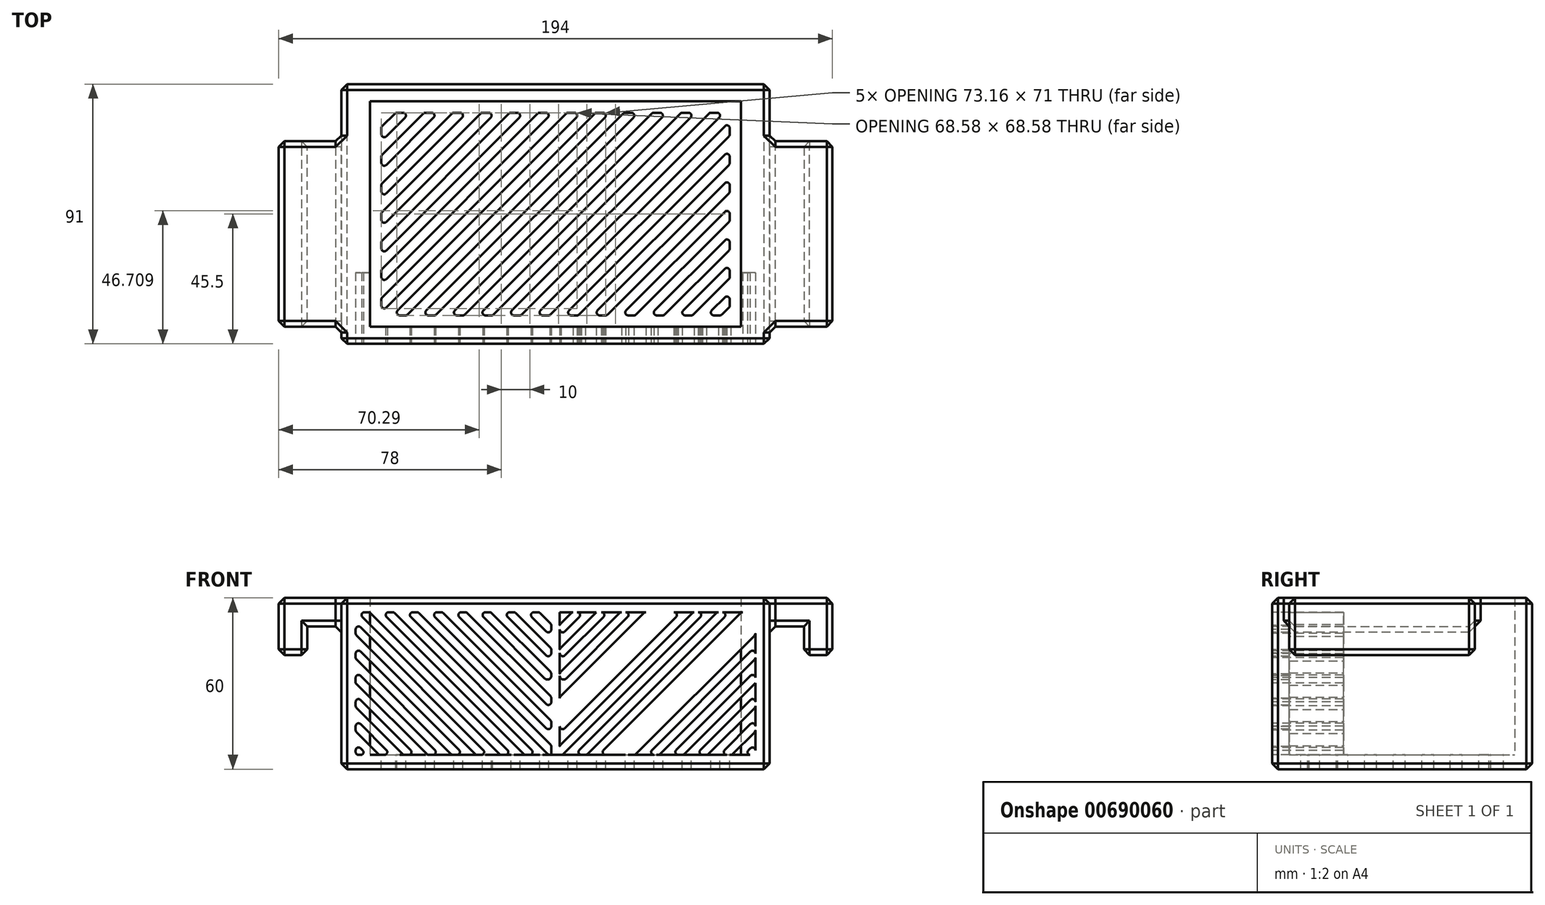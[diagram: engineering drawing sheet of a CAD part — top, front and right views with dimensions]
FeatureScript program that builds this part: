
annotation { "Feature Type Name" : "Feature", "Feature Type Description" : "" }
export const myFeature = defineFeature(function(context is Context, id is Id, definition is map)
    precondition{}
    {
        {
            var Q0;
            Q0=qCreatedBy(makeId("Top.planeOp"),FACE);
            var sketch = newSketch(context, id + "F0", { "sketchPlane" : qUnion([Q0])});
            skLineSegment(sketch, "E0", {"start": v(0, 0) * mm, "end": v(0, -65) * mm});
            skLineSegment(sketch, "E1", {"start": v(0, -65) * mm, "end": v(12, -65) * mm});
            skLineSegment(sketch, "E2", {"start": v(12, -65) * mm, "end": v(12, 0) * mm});
            skLineSegment(sketch, "E3", {"start": v(12, 0) * mm, "end": v(0, 0) * mm});
            skLineSegment(sketch, "E4", {"start": v(12, -65) * mm, "end": v(22, -65) * mm});
            skLineSegment(sketch, "E5", {"start": v(22, -65) * mm, "end": v(22, 0) * mm});
            skLineSegment(sketch, "E6", {"start": v(22, 0) * mm, "end": v(12, 0) * mm});
            skLineSegment(sketch, "E7", {"start": v(0, -65) * mm, "end": v(-10, -65) * mm});
            skLineSegment(sketch, "E8", {"start": v(-10, -65) * mm, "end": v(-10, 20) * mm});
            skLineSegment(sketch, "E9", {"start": v(-10, 20) * mm, "end": v(0, 20) * mm});
            skLineSegment(sketch, "E10", {"start": v(0, 20) * mm, "end": v(0, 0) * mm});
            skLineSegment(sketch, "E11", {"start": v(-10, 20) * mm, "end": v(-140, 20) * mm});
            skLineSegment(sketch, "E12.MirrorCS", {"start": v(-150, 0) * mm, "end": v(-150, -65) * mm});
            skLineSegment(sketch, "E13.MirrorCS", {"start": v(-150, -65) * mm, "end": v(-162, -65) * mm});
            skLineSegment(sketch, "E14.MirrorCS", {"start": v(-162, -65) * mm, "end": v(-162, 0) * mm});
            skLineSegment(sketch, "E15.MirrorCS", {"start": v(-150, 20) * mm, "end": v(-150, 0) * mm});
            skLineSegment(sketch, "E16.MirrorCS", {"start": v(-140, 20) * mm, "end": v(-150, 20) * mm});
            skLineSegment(sketch, "E17.MirrorCS", {"start": v(-140, -65) * mm, "end": v(-140, 20) * mm});
            skLineSegment(sketch, "E18.MirrorCS", {"start": v(-150, -65) * mm, "end": v(-140, -65) * mm});
            skLineSegment(sketch, "E19.MirrorCS", {"start": v(-172, 0) * mm, "end": v(-162, 0) * mm});
            skLineSegment(sketch, "E20.MirrorCS", {"start": v(-172, -65) * mm, "end": v(-172, 0) * mm});
            skLineSegment(sketch, "E21.MirrorCS", {"start": v(-162, -65) * mm, "end": v(-172, -65) * mm});
            skLineSegment(sketch, "E22.MirrorCS", {"start": v(-162, 0) * mm, "end": v(-150, 0) * mm});
            skLineSegment(sketch, "E23", {"start": v(-140, -65) * mm, "end": v(-10, -65) * mm});
            skLineSegment(sketch, "E24", {"start": v(-150, -65) * mm, "end": v(-150, -71) * mm});
            skLineSegment(sketch, "E25", {"start": v(-150, -71) * mm, "end": v(0, -71) * mm});
            skLineSegment(sketch, "E26", {"start": v(0, -71) * mm, "end": v(0, -65) * mm});
            skLineSegment(sketch, "E27", {"start": v(-140, 14) * mm, "end": v(-10, 14) * mm});
            skSolve(sketch);
        }
        {
            var Q0;
            Q0=makeQuery(id+"F0.imprint","IMPRINT",FACE,{"disambiguationData":[TD([[makeQuery(id+"F0.imprint","IMPRINT",EDGE,{"derivedFrom":sQuery(id+"F0.wireOp",EDGE,"E14.MirrorCS")}),1.0]])]});
            var Q1;
            Q1=makeQuery(id+"F0.imprint","IMPRINT",FACE,{"disambiguationData":[TD([[makeQuery(id+"F0.imprint","IMPRINT",EDGE,{"derivedFrom":sQuery(id+"F0.wireOp",EDGE,"E2")}),-1.0]])]});
            extrude(context, id + "F1", {"entities" : qUnion([Q0, Q1]), "oppositeDirection" : true, "depth" : 10 * mm, "offsetDistance" : 25 * mm, "hasSecondDirection" : true, "secondDirectionOppositeDirection" : false, "secondDirectionDepth" : 10 * mm});
        }
        {
            var Q0;
            Q0=makeQuery(id+"F0.imprint","IMPRINT",FACE,{"disambiguationData":[TD([[makeQuery(id+"F0.imprint","IMPRINT",EDGE,{"derivedFrom":sQuery(id+"F0.wireOp",EDGE,"E12.MirrorCS")}),-1.0]])]});
            var Q1;
            Q1=makeQuery(id+"F0.imprint","IMPRINT",FACE,{"disambiguationData":[TD([[makeQuery(id+"F0.imprint","IMPRINT",EDGE,{"derivedFrom":sQuery(id+"F0.wireOp",EDGE,"E0")}),1.0]])]});
            extrude(context, id + "F2", {"entities" : qUnion([Q0, Q1]), "operationType" : NewBodyOperationType.ADD, "depth" : 10 * mm, "offsetDistance" : 25 * mm});
        }
        {
            var Q0;
            Q0=makeQuery(id+"F0.imprint","IMPRINT",FACE,{"disambiguationData":[TD([[makeQuery(id+"F0.imprint","IMPRINT",EDGE,{"derivedFrom":sQuery(id+"F0.wireOp",EDGE,"E12.MirrorCS")}),1.0]])]});
            var Q1;
            Q1=makeQuery(id+"F0.imprint","IMPRINT",FACE,{"disambiguationData":[TD([[makeQuery(id+"F0.imprint","IMPRINT",EDGE,{"derivedFrom":sQuery(id+"F0.wireOp",EDGE,"E0")}),-1.0]])]});
            extrude(context, id + "F3", {"entities" : qUnion([Q0, Q1]), "operationType" : NewBodyOperationType.ADD, "depth" : 10 * mm, "offsetDistance" : 25 * mm, "hasSecondDirection" : true, "secondDirectionOppositeDirection" : true, "secondDirectionDepth" : 50 * mm});
        }
        {
            var Q0;
            Q0=makeQuery(id+"F0.imprint","IMPRINT",FACE,{"disambiguationData":[TD([[makeQuery(id+"F0.imprint","IMPRINT",EDGE,{"derivedFrom":sQuery(id+"F0.wireOp",EDGE,"E7")}),1.0]])]});
            extrude(context, id + "F4", {"entities" : qUnion([Q0]), "operationType" : NewBodyOperationType.ADD, "depth" : 10 * mm, "offsetDistance" : 25 * mm, "hasSecondDirection" : true, "secondDirectionOppositeDirection" : true, "secondDirectionDepth" : 50 * mm});
        }
        {
            var Q0;
            {var subQ0=sQuery(id+"F0.wireOp",EDGE,"E11");Q0=makeQuery(id+"F0.imprint","IMPRINT",FACE,{"disambiguationData":[TD([[makeQuery(id+"F0.imprint","IMPRINT",EDGE,{"derivedFrom":subQ0}),1.0]])]});}
            extrude(context, id + "F5", {"entities" : qUnion([Q0]), "operationType" : NewBodyOperationType.ADD, "depth" : 10 * mm, "offsetDistance" : 25 * mm, "hasSecondDirection" : true, "secondDirectionOppositeDirection" : true, "secondDirectionDepth" : 50 * mm});
        }
        {
            var Q0;
            {var subQ0=sQuery(id+"F0.wireOp",EDGE,"E23");Q0=makeQuery(id+"F0.imprint","IMPRINT",FACE,{"disambiguationData":[TD([[makeQuery(id+"F0.imprint","IMPRINT",EDGE,{"derivedFrom":subQ0}),1.0]])]});}
            extrude(context, id + "F6", {"entities" : qUnion([Q0]), "operationType" : NewBodyOperationType.ADD, "oppositeDirection" : true, "depth" : 50 * mm, "offsetDistance" : 25 * mm, "hasSecondDirection" : true, "secondDirectionOppositeDirection" : true, "secondDirectionDepth" : 45 * mm});
        }
        {
            var Q0;
            {var subQ0=sQuery(id+"F0.wireOp",EDGE,"E23");Q0=makeQuery(id+"F0.imprint","IMPRINT",FACE,{"disambiguationData":[TD([[makeQuery(id+"F0.imprint","IMPRINT",EDGE,{"derivedFrom":subQ0}),1.0]])]});}
            var sketch = newSketch(context, id + "F7", { "sketchPlane" : qUnion([Q0])});
            skLineSegment(sketch, "E28.0.0", {"start": v(-140, 14) * mm, "end": v(-140, -65) * mm});
            skLineSegment(sketch, "E28.0.1", {"start": v(-140, -65) * mm, "end": v(-10, -65) * mm});
            skLineSegment(sketch, "E28.0.2", {"start": v(-10, -65) * mm, "end": v(-10, 14) * mm});
            skLineSegment(sketch, "E28.0.3", {"start": v(-10, 14) * mm, "end": v(-140, 14) * mm});
            skLineSegment(sketch, "E29.0", {"start": v(-18.41, 10) * mm, "end": v(-20.59, 10) * mm});
            skLineSegment(sketch, "E29.1", {"start": v(-14, -58) * mm, "end": v(-14, -55.41) * mm});
            skLineSegment(sketch, "E29.2", {"start": v(-129.59, -61) * mm, "end": v(-127.41, -61) * mm});
            skLineSegment(sketch, "E29.3", {"start": v(-136, 5) * mm, "end": v(-136, 2.41) * mm});
            skLineSegment(sketch, "E30", {"start": v(-136, 5) * mm, "end": v(-131, 10) * mm});
            skLineSegment(sketch, "E31.1.0.0", {"start": v(-134.3, 1.7) * mm, "end": v(-127.7, 8.3) * mm});
            skLineSegment(sketch, "E31.2.0.0", {"start": v(-135.7, -4.7) * mm, "end": v(-121.3, 9.7) * mm});
            skLineSegment(sketch, "E31.3.0.0", {"start": v(-134.3, -8.3) * mm, "end": v(-117.7, 8.3) * mm});
            skLineSegment(sketch, "E31.4.0.0", {"start": v(-135.7, -14.7) * mm, "end": v(-111.3, 9.7) * mm});
            skLineSegment(sketch, "E31.5.0.0", {"start": v(-134.3, -18.3) * mm, "end": v(-107.7, 8.3) * mm});
            skLineSegment(sketch, "E31.6.0.0", {"start": v(-135.7, -24.7) * mm, "end": v(-101.3, 9.7) * mm});
            skLineSegment(sketch, "E31.7.0.0", {"start": v(-134.3, -28.3) * mm, "end": v(-97.7, 8.3) * mm});
            skLineSegment(sketch, "E31.8.0.0", {"start": v(-135.7, -34.7) * mm, "end": v(-91.3, 9.7) * mm});
            skLineSegment(sketch, "E31.9.0.0", {"start": v(-134.3, -38.3) * mm, "end": v(-87.7, 8.3) * mm});
            skLineSegment(sketch, "E31.10.0.0", {"start": v(-135.7, -44.7) * mm, "end": v(-81.3, 9.7) * mm});
            skLineSegment(sketch, "E31.11.0.0", {"start": v(-134.3, -48.3) * mm, "end": v(-77.7, 8.3) * mm});
            skLineSegment(sketch, "E31.12.0.0", {"start": v(-135.7, -54.7) * mm, "end": v(-71.3, 9.7) * mm});
            skLineSegment(sketch, "E31.13.0.0", {"start": v(-134.3, -58.3) * mm, "end": v(-67.7, 8.3) * mm});
            skLineSegment(sketch, "E31.14.0.0", {"start": v(-130.3, -59.3) * mm, "end": v(-61.3, 9.7) * mm});
            skLineSegment(sketch, "E31.15.0.0", {"start": v(-126.7, -60.7) * mm, "end": v(-57.7, 8.3) * mm});
            skLineSegment(sketch, "E31.16.0.0", {"start": v(-120.3, -59.3) * mm, "end": v(-51.3, 9.7) * mm});
            skLineSegment(sketch, "E31.17.0.0", {"start": v(-116.7, -60.7) * mm, "end": v(-47.7, 8.3) * mm});
            skLineSegment(sketch, "E31.18.0.0", {"start": v(-110.3, -59.3) * mm, "end": v(-41.3, 9.7) * mm});
            skLineSegment(sketch, "E31.19.0.0", {"start": v(-106.7, -60.7) * mm, "end": v(-37.7, 8.3) * mm});
            skLineSegment(sketch, "E31.direction1", {"start": v(-136, 5) * mm, "end": v(-131, 5) * mm, "construction": true});
            skLineSegment(sketch, "E32.1.0.0", {"start": v(-100.3, -59.3) * mm, "end": v(-31.3, 9.7) * mm});
            skLineSegment(sketch, "E32.2.0.0", {"start": v(-97, -61) * mm, "end": v(-27.7, 8.3) * mm});
            skLineSegment(sketch, "E32.3.0.0", {"start": v(-90.3, -59.3) * mm, "end": v(-21.3, 9.7) * mm});
            skLineSegment(sketch, "E32.4.0.0", {"start": v(-86.7, -60.7) * mm, "end": v(-17.7, 8.3) * mm});
            skPoint(sketch, "E33.orphan", {"position": v(-126, 5) * mm});
            skPoint(sketch, "E34.orphan", {"position": v(-121, 5) * mm});
            skPoint(sketch, "E35.orphan", {"position": v(-116, 5) * mm});
            skPoint(sketch, "E36.orphan", {"position": v(-111, 5) * mm});
            skPoint(sketch, "E37.orphan", {"position": v(-106, 5) * mm});
            skPoint(sketch, "E38.orphan", {"position": v(-101, 5) * mm});
            skPoint(sketch, "E39.orphan", {"position": v(-96, 5) * mm});
            skPoint(sketch, "E40.orphan", {"position": v(-91, 5) * mm});
            skPoint(sketch, "E41.orphan", {"position": v(-86, 5) * mm});
            skPoint(sketch, "E42.orphan", {"position": v(-81, 5) * mm});
            skPoint(sketch, "E43.orphan", {"position": v(-76, 5) * mm});
            skPoint(sketch, "E44.orphan", {"position": v(-71, 5) * mm});
            skPoint(sketch, "E45.orphan", {"position": v(-66, 5) * mm});
            skPoint(sketch, "E46.orphan", {"position": v(-61, 5) * mm});
            skPoint(sketch, "E47.orphan", {"position": v(-56, 5) * mm});
            skPoint(sketch, "E48.orphan", {"position": v(-51, 5) * mm});
            skLineSegment(sketch, "E49.1.0.0", {"start": v(-80.3, -59.3) * mm, "end": v(-15.7, 5.3) * mm});
            skLineSegment(sketch, "E49.2.0.0", {"start": v(-76.7, -60.7) * mm, "end": v(-14.3, 1.7) * mm});
            skLineSegment(sketch, "E49.3.0.0", {"start": v(-70.3, -59.3) * mm, "end": v(-15.7, -4.7) * mm});
            skLineSegment(sketch, "E49.4.0.0", {"start": v(-66.7, -60.7) * mm, "end": v(-14.3, -8.3) * mm});
            skLineSegment(sketch, "E49.5.0.0", {"start": v(-60.3, -59.3) * mm, "end": v(-15.7, -14.7) * mm});
            skLineSegment(sketch, "E49.6.0.0", {"start": v(-56.7, -60.7) * mm, "end": v(-14.3, -18.3) * mm});
            skLineSegment(sketch, "E49.7.0.0", {"start": v(-50.3, -59.3) * mm, "end": v(-15.7, -24.7) * mm});
            skLineSegment(sketch, "E49.8.0.0", {"start": v(-46.7, -60.7) * mm, "end": v(-14.3, -28.3) * mm});
            skLineSegment(sketch, "E49.9.0.0", {"start": v(-40.3, -59.3) * mm, "end": v(-15.7, -34.7) * mm});
            skLineSegment(sketch, "E49.10.0.0", {"start": v(-36.7, -60.7) * mm, "end": v(-14.3, -38.3) * mm});
            skLineSegment(sketch, "E49.11.0.0", {"start": v(-30.3, -59.3) * mm, "end": v(-15.7, -44.7) * mm});
            skLineSegment(sketch, "E49.12.0.0", {"start": v(-26.7, -60.7) * mm, "end": v(-14, -48) * mm});
            skLineSegment(sketch, "E49.13.0.0", {"start": v(-20.3, -59.3) * mm, "end": v(-15.7, -54.7) * mm});
            skLineSegment(sketch, "E49.14.0.0", {"start": v(-16.7, -60.7) * mm, "end": v(-14, -58) * mm});
            skPoint(sketch, "E50.orphan", {"position": v(-136, 10) * mm});
            skLineSegment(sketch, "E51.trimOffspring", {"start": v(-136, -5.41) * mm, "end": v(-136, -7.59) * mm});
            skLineSegment(sketch, "E52.trimOffspring", {"start": v(-136, -15.41) * mm, "end": v(-136, -17.59) * mm});
            skLineSegment(sketch, "E53.trimOffspring", {"start": v(-128.41, 10) * mm, "end": v(-131, 10) * mm});
            skLineSegment(sketch, "E54.trimOffspring", {"start": v(-118.41, 10) * mm, "end": v(-120.59, 10) * mm});
            skLineSegment(sketch, "E55.trimOffspring", {"start": v(-108.41, 10) * mm, "end": v(-110.59, 10) * mm});
            skLineSegment(sketch, "E56.trimOffspring", {"start": v(-98.41, 10) * mm, "end": v(-100.59, 10) * mm});
            skLineSegment(sketch, "E57.trimOffspring", {"start": v(-88.41, 10) * mm, "end": v(-90.59, 10) * mm});
            skLineSegment(sketch, "E58.trimOffspring", {"start": v(-78.41, 10) * mm, "end": v(-80.59, 10) * mm});
            skLineSegment(sketch, "E59.trimOffspring", {"start": v(-68.41, 10) * mm, "end": v(-70.59, 10) * mm});
            skLineSegment(sketch, "E60.trimOffspring", {"start": v(-136, -25.41) * mm, "end": v(-136, -27.59) * mm});
            skLineSegment(sketch, "E61.trimOffspring", {"start": v(-136, -35.41) * mm, "end": v(-136, -37.59) * mm});
            skLineSegment(sketch, "E62.trimOffspring", {"start": v(-136, -45.41) * mm, "end": v(-136, -47.59) * mm});
            skLineSegment(sketch, "E63.trimOffspring", {"start": v(-136, -55.41) * mm, "end": v(-136, -57.59) * mm});
            skLineSegment(sketch, "E64.trimOffspring", {"start": v(-119.59, -61) * mm, "end": v(-117.41, -61) * mm});
            skLineSegment(sketch, "E65.trimOffspring", {"start": v(-109.59, -61) * mm, "end": v(-107.41, -61) * mm});
            skLineSegment(sketch, "E66.trimOffspring", {"start": v(-99.59, -61) * mm, "end": v(-97, -61) * mm});
            skLineSegment(sketch, "E67.trimOffspring", {"start": v(-89.59, -61) * mm, "end": v(-87.41, -61) * mm});
            skLineSegment(sketch, "E68.trimOffspring", {"start": v(-58.41, 10) * mm, "end": v(-60.59, 10) * mm});
            skLineSegment(sketch, "E69.trimOffspring", {"start": v(-48.41, 10) * mm, "end": v(-50.59, 10) * mm});
            skLineSegment(sketch, "E70.trimOffspring", {"start": v(-14, 2.41) * mm, "end": v(-14, 4.59) * mm});
            skLineSegment(sketch, "E71.trimOffspring", {"start": v(-14, -7.59) * mm, "end": v(-14, -5.41) * mm});
            skLineSegment(sketch, "E72.trimOffspring", {"start": v(-14, -17.59) * mm, "end": v(-14, -15.41) * mm});
            skLineSegment(sketch, "E73.trimOffspring", {"start": v(-14, -27.59) * mm, "end": v(-14, -25.41) * mm});
            skLineSegment(sketch, "E74.trimOffspring", {"start": v(-14, -37.59) * mm, "end": v(-14, -35.41) * mm});
            skLineSegment(sketch, "E75.trimOffspring", {"start": v(-14, -48) * mm, "end": v(-14, -45.41) * mm});
            skLineSegment(sketch, "E76.trimOffspring", {"start": v(-19.59, -61) * mm, "end": v(-17.41, -61) * mm});
            skLineSegment(sketch, "E77.trimOffspring", {"start": v(-29.59, -61) * mm, "end": v(-27.41, -61) * mm});
            skLineSegment(sketch, "E78.trimOffspring", {"start": v(-39.59, -61) * mm, "end": v(-37.41, -61) * mm});
            skLineSegment(sketch, "E79.trimOffspring", {"start": v(-49.59, -61) * mm, "end": v(-47.41, -61) * mm});
            skLineSegment(sketch, "E80.trimOffspring", {"start": v(-59.59, -61) * mm, "end": v(-57.41, -61) * mm});
            skLineSegment(sketch, "E81.trimOffspring", {"start": v(-69.59, -61) * mm, "end": v(-67.41, -61) * mm});
            skLineSegment(sketch, "E82.trimOffspring", {"start": v(-79.59, -61) * mm, "end": v(-77.41, -61) * mm});
            skLineSegment(sketch, "E83", {"start": v(-40.59, 10) * mm, "end": v(-38.41, 10) * mm});
            skLineSegment(sketch, "E84", {"start": v(-30.59, 10) * mm, "end": v(-28.41, 10) * mm});
            skPoint(sketch, "E85.visualSharp", {"position": v(-126, 10) * mm});
            skArc(sketch, "E85.filletArc", {"start": v(-127.7, 8.3) * mm, "mid": v(-127.5, 9.38) * mm, "end": v(-128.41, 10) * mm});
            skPoint(sketch, "E86.visualSharp", {"position": v(-136, 0) * mm});
            skArc(sketch, "E86.filletArc", {"start": v(-136, 2.41) * mm, "mid": v(-135.38, 1.5) * mm, "end": v(-134.3, 1.7) * mm});
            skPoint(sketch, "E87.visualSharp", {"position": v(-116, 10) * mm});
            skArc(sketch, "E87.filletArc", {"start": v(-117.7, 8.3) * mm, "mid": v(-117.5, 9.38) * mm, "end": v(-118.41, 10) * mm});
            skPoint(sketch, "E88.visualSharp", {"position": v(-136, -10) * mm});
            skArc(sketch, "E88.filletArc", {"start": v(-136, -7.59) * mm, "mid": v(-135.38, -8.5) * mm, "end": v(-134.3, -8.3) * mm});
            skPoint(sketch, "E89.visualSharp", {"position": v(-136, -5) * mm});
            skArc(sketch, "E89.filletArc", {"start": v(-135.7, -4.7) * mm, "mid": v(-135.92, -5.03) * mm, "end": v(-136, -5.41) * mm});
            skPoint(sketch, "E90.visualSharp", {"position": v(-121, 10) * mm});
            skArc(sketch, "E90.filletArc", {"start": v(-120.59, 10) * mm, "mid": v(-120.97, 9.92) * mm, "end": v(-121.3, 9.7) * mm});
            skPoint(sketch, "E91.visualSharp", {"position": v(-111, 10) * mm});
            skArc(sketch, "E91.filletArc", {"start": v(-110.59, 10) * mm, "mid": v(-110.97, 9.92) * mm, "end": v(-111.3, 9.7) * mm});
            skPoint(sketch, "E92.visualSharp", {"position": v(-106, 10) * mm});
            skArc(sketch, "E92.filletArc", {"start": v(-107.7, 8.3) * mm, "mid": v(-107.5, 9.38) * mm, "end": v(-108.41, 10) * mm});
            skPoint(sketch, "E93.visualSharp", {"position": v(-136, -20) * mm});
            skArc(sketch, "E93.filletArc", {"start": v(-136, -17.59) * mm, "mid": v(-135.38, -18.5) * mm, "end": v(-134.3, -18.3) * mm});
            skPoint(sketch, "E94.visualSharp", {"position": v(-136, -15) * mm});
            skArc(sketch, "E94.filletArc", {"start": v(-135.7, -14.7) * mm, "mid": v(-135.92, -15.03) * mm, "end": v(-136, -15.41) * mm});
            skPoint(sketch, "E95.visualSharp", {"position": v(-136, -25) * mm});
            skArc(sketch, "E95.filletArc", {"start": v(-135.7, -24.7) * mm, "mid": v(-135.92, -25.03) * mm, "end": v(-136, -25.41) * mm});
            skPoint(sketch, "E96.visualSharp", {"position": v(-136, -30) * mm});
            skArc(sketch, "E96.filletArc", {"start": v(-136, -27.59) * mm, "mid": v(-135.38, -28.5) * mm, "end": v(-134.3, -28.3) * mm});
            skPoint(sketch, "E97.visualSharp", {"position": v(-101, 10) * mm});
            skArc(sketch, "E97.filletArc", {"start": v(-100.59, 10) * mm, "mid": v(-100.97, 9.92) * mm, "end": v(-101.3, 9.7) * mm});
            skPoint(sketch, "E98.visualSharp", {"position": v(-96, 10) * mm});
            skArc(sketch, "E98.filletArc", {"start": v(-97.7, 8.3) * mm, "mid": v(-97.5, 9.38) * mm, "end": v(-98.41, 10) * mm});
            skPoint(sketch, "E99.visualSharp", {"position": v(-91, 10) * mm});
            skArc(sketch, "E99.filletArc", {"start": v(-90.59, 10) * mm, "mid": v(-90.97, 9.92) * mm, "end": v(-91.3, 9.7) * mm});
            skPoint(sketch, "E100.visualSharp", {"position": v(-86, 10) * mm});
            skArc(sketch, "E100.filletArc", {"start": v(-87.7, 8.3) * mm, "mid": v(-87.5, 9.38) * mm, "end": v(-88.41, 10) * mm});
            skPoint(sketch, "E101.visualSharp", {"position": v(-136, -40) * mm});
            skArc(sketch, "E101.filletArc", {"start": v(-136, -37.59) * mm, "mid": v(-135.38, -38.5) * mm, "end": v(-134.3, -38.3) * mm});
            skPoint(sketch, "E102.visualSharp", {"position": v(-136, -35) * mm});
            skArc(sketch, "E102.filletArc", {"start": v(-135.7, -34.7) * mm, "mid": v(-135.92, -35.03) * mm, "end": v(-136, -35.41) * mm});
            skPoint(sketch, "E103.visualSharp", {"position": v(-136, -45) * mm});
            skArc(sketch, "E103.filletArc", {"start": v(-135.7, -44.7) * mm, "mid": v(-135.92, -45.03) * mm, "end": v(-136, -45.41) * mm});
            skPoint(sketch, "E104.visualSharp", {"position": v(-136, -50) * mm});
            skArc(sketch, "E104.filletArc", {"start": v(-136, -47.59) * mm, "mid": v(-135.38, -48.5) * mm, "end": v(-134.3, -48.3) * mm});
            skPoint(sketch, "E105.visualSharp", {"position": v(-136, -55) * mm});
            skArc(sketch, "E105.filletArc", {"start": v(-135.7, -54.7) * mm, "mid": v(-135.92, -55.03) * mm, "end": v(-136, -55.41) * mm});
            skPoint(sketch, "E106.visualSharp", {"position": v(-136, -60) * mm});
            skArc(sketch, "E106.filletArc", {"start": v(-136, -57.59) * mm, "mid": v(-135.38, -58.5) * mm, "end": v(-134.3, -58.3) * mm});
            skPoint(sketch, "E107.visualSharp", {"position": v(-132, -61) * mm});
            skArc(sketch, "E107.filletArc", {"start": v(-130.3, -59.3) * mm, "mid": v(-130.5, -60.38) * mm, "end": v(-129.59, -61) * mm});
            skPoint(sketch, "E108.visualSharp", {"position": v(-127, -61) * mm});
            skArc(sketch, "E108.filletArc", {"start": v(-127.41, -61) * mm, "mid": v(-127.03, -60.92) * mm, "end": v(-126.7, -60.7) * mm});
            skPoint(sketch, "E109.visualSharp", {"position": v(-81, 10) * mm});
            skArc(sketch, "E109.filletArc", {"start": v(-80.59, 10) * mm, "mid": v(-80.97, 9.92) * mm, "end": v(-81.3, 9.7) * mm});
            skPoint(sketch, "E110.visualSharp", {"position": v(-76, 10) * mm});
            skArc(sketch, "E110.filletArc", {"start": v(-77.7, 8.3) * mm, "mid": v(-77.5, 9.38) * mm, "end": v(-78.41, 10) * mm});
            skPoint(sketch, "E111.visualSharp", {"position": v(-71, 10) * mm});
            skArc(sketch, "E111.filletArc", {"start": v(-70.59, 10) * mm, "mid": v(-70.97, 9.92) * mm, "end": v(-71.3, 9.7) * mm});
            skPoint(sketch, "E112.visualSharp", {"position": v(-66, 10) * mm});
            skArc(sketch, "E112.filletArc", {"start": v(-67.7, 8.3) * mm, "mid": v(-67.5, 9.38) * mm, "end": v(-68.41, 10) * mm});
            skPoint(sketch, "E113.visualSharp", {"position": v(-61, 10) * mm});
            skArc(sketch, "E113.filletArc", {"start": v(-60.59, 10) * mm, "mid": v(-60.97, 9.92) * mm, "end": v(-61.3, 9.7) * mm});
            skPoint(sketch, "E114.visualSharp", {"position": v(-56, 10) * mm});
            skArc(sketch, "E114.filletArc", {"start": v(-57.7, 8.3) * mm, "mid": v(-57.5, 9.38) * mm, "end": v(-58.41, 10) * mm});
            skPoint(sketch, "E115.visualSharp", {"position": v(-51, 10) * mm});
            skArc(sketch, "E115.filletArc", {"start": v(-50.59, 10) * mm, "mid": v(-50.97, 9.92) * mm, "end": v(-51.3, 9.7) * mm});
            skPoint(sketch, "E116.visualSharp", {"position": v(-46, 10) * mm});
            skArc(sketch, "E116.filletArc", {"start": v(-47.7, 8.3) * mm, "mid": v(-47.5, 9.38) * mm, "end": v(-48.41, 10) * mm});
            skPoint(sketch, "E117.visualSharp", {"position": v(-41, 10) * mm});
            skArc(sketch, "E117.filletArc", {"start": v(-40.59, 10) * mm, "mid": v(-40.97, 9.92) * mm, "end": v(-41.3, 9.7) * mm});
            skPoint(sketch, "E118.visualSharp", {"position": v(-36, 10) * mm});
            skArc(sketch, "E118.filletArc", {"start": v(-37.7, 8.3) * mm, "mid": v(-37.5, 9.38) * mm, "end": v(-38.41, 10) * mm});
            skPoint(sketch, "E119.visualSharp", {"position": v(-31, 10) * mm});
            skArc(sketch, "E119.filletArc", {"start": v(-30.59, 10) * mm, "mid": v(-30.97, 9.92) * mm, "end": v(-31.3, 9.7) * mm});
            skPoint(sketch, "E120.visualSharp", {"position": v(-26, 10) * mm});
            skArc(sketch, "E120.filletArc", {"start": v(-27.7, 8.3) * mm, "mid": v(-27.5, 9.38) * mm, "end": v(-28.41, 10) * mm});
            skPoint(sketch, "E121.visualSharp", {"position": v(-21, 10) * mm});
            skArc(sketch, "E121.filletArc", {"start": v(-20.59, 10) * mm, "mid": v(-20.97, 9.92) * mm, "end": v(-21.3, 9.7) * mm});
            skPoint(sketch, "E122.visualSharp", {"position": v(-16, 10) * mm});
            skArc(sketch, "E122.filletArc", {"start": v(-17.7, 8.3) * mm, "mid": v(-17.5, 9.38) * mm, "end": v(-18.41, 10) * mm});
            skPoint(sketch, "E123.visualSharp", {"position": v(-14, 7) * mm});
            skArc(sketch, "E123.filletArc", {"start": v(-14, 4.59) * mm, "mid": v(-14.62, 5.5) * mm, "end": v(-15.7, 5.3) * mm});
            skPoint(sketch, "E124.visualSharp", {"position": v(-14, 2) * mm});
            skArc(sketch, "E124.filletArc", {"start": v(-14.3, 1.7) * mm, "mid": v(-14.08, 2.03) * mm, "end": v(-14, 2.41) * mm});
            skPoint(sketch, "E125.visualSharp", {"position": v(-14, -3) * mm});
            skArc(sketch, "E125.filletArc", {"start": v(-14, -5.41) * mm, "mid": v(-14.62, -4.5) * mm, "end": v(-15.7, -4.7) * mm});
            skPoint(sketch, "E126.visualSharp", {"position": v(-14, -8) * mm});
            skArc(sketch, "E126.filletArc", {"start": v(-14.3, -8.3) * mm, "mid": v(-14.08, -7.97) * mm, "end": v(-14, -7.59) * mm});
            skPoint(sketch, "E127.visualSharp", {"position": v(-14, -13) * mm});
            skArc(sketch, "E127.filletArc", {"start": v(-14, -15.41) * mm, "mid": v(-14.62, -14.5) * mm, "end": v(-15.7, -14.7) * mm});
            skPoint(sketch, "E128.visualSharp", {"position": v(-14, -18) * mm});
            skArc(sketch, "E128.filletArc", {"start": v(-14.3, -18.3) * mm, "mid": v(-14.08, -17.97) * mm, "end": v(-14, -17.59) * mm});
            skPoint(sketch, "E129.visualSharp", {"position": v(-14, -23) * mm});
            skArc(sketch, "E129.filletArc", {"start": v(-14, -25.41) * mm, "mid": v(-14.62, -24.5) * mm, "end": v(-15.7, -24.7) * mm});
            skPoint(sketch, "E130.visualSharp", {"position": v(-14, -28) * mm});
            skArc(sketch, "E130.filletArc", {"start": v(-14.3, -28.3) * mm, "mid": v(-14.08, -27.97) * mm, "end": v(-14, -27.59) * mm});
            skPoint(sketch, "E131.visualSharp", {"position": v(-14, -33) * mm});
            skArc(sketch, "E131.filletArc", {"start": v(-14, -35.41) * mm, "mid": v(-14.62, -34.5) * mm, "end": v(-15.7, -34.7) * mm});
            skPoint(sketch, "E132.visualSharp", {"position": v(-14, -38) * mm});
            skArc(sketch, "E132.filletArc", {"start": v(-14.3, -38.3) * mm, "mid": v(-14.08, -37.97) * mm, "end": v(-14, -37.59) * mm});
            skPoint(sketch, "E133.visualSharp", {"position": v(-14, -43) * mm});
            skArc(sketch, "E133.filletArc", {"start": v(-14, -45.41) * mm, "mid": v(-14.62, -44.5) * mm, "end": v(-15.7, -44.7) * mm});
            skPoint(sketch, "E134.visualSharp", {"position": v(-14, -53) * mm});
            skArc(sketch, "E134.filletArc", {"start": v(-14, -55.41) * mm, "mid": v(-14.62, -54.5) * mm, "end": v(-15.7, -54.7) * mm});
            skPoint(sketch, "E135.visualSharp", {"position": v(-17, -61) * mm});
            skArc(sketch, "E135.filletArc", {"start": v(-17.41, -61) * mm, "mid": v(-17.03, -60.92) * mm, "end": v(-16.7, -60.7) * mm});
            skPoint(sketch, "E136.visualSharp", {"position": v(-22, -61) * mm});
            skArc(sketch, "E136.filletArc", {"start": v(-20.3, -59.3) * mm, "mid": v(-20.5, -60.38) * mm, "end": v(-19.59, -61) * mm});
            skPoint(sketch, "E137.visualSharp", {"position": v(-27, -61) * mm});
            skArc(sketch, "E137.filletArc", {"start": v(-27.41, -61) * mm, "mid": v(-27.03, -60.92) * mm, "end": v(-26.7, -60.7) * mm});
            skPoint(sketch, "E138.visualSharp", {"position": v(-32, -61) * mm});
            skArc(sketch, "E138.filletArc", {"start": v(-30.3, -59.3) * mm, "mid": v(-30.5, -60.38) * mm, "end": v(-29.59, -61) * mm});
            skPoint(sketch, "E139.visualSharp", {"position": v(-37, -61) * mm});
            skArc(sketch, "E139.filletArc", {"start": v(-37.41, -61) * mm, "mid": v(-37.03, -60.92) * mm, "end": v(-36.7, -60.7) * mm});
            skPoint(sketch, "E140.visualSharp", {"position": v(-42, -61) * mm});
            skArc(sketch, "E140.filletArc", {"start": v(-40.3, -59.3) * mm, "mid": v(-40.5, -60.38) * mm, "end": v(-39.59, -61) * mm});
            skPoint(sketch, "E141.visualSharp", {"position": v(-47, -61) * mm});
            skArc(sketch, "E141.filletArc", {"start": v(-47.41, -61) * mm, "mid": v(-47.03, -60.92) * mm, "end": v(-46.7, -60.7) * mm});
            skPoint(sketch, "E142.visualSharp", {"position": v(-52, -61) * mm});
            skArc(sketch, "E142.filletArc", {"start": v(-50.3, -59.3) * mm, "mid": v(-50.5, -60.38) * mm, "end": v(-49.59, -61) * mm});
            skPoint(sketch, "E143.visualSharp", {"position": v(-62, -61) * mm});
            skArc(sketch, "E143.filletArc", {"start": v(-60.3, -59.3) * mm, "mid": v(-60.5, -60.38) * mm, "end": v(-59.59, -61) * mm});
            skPoint(sketch, "E144.visualSharp", {"position": v(-57, -61) * mm});
            skArc(sketch, "E144.filletArc", {"start": v(-57.41, -61) * mm, "mid": v(-57.03, -60.92) * mm, "end": v(-56.7, -60.7) * mm});
            skPoint(sketch, "E145.visualSharp", {"position": v(-67, -61) * mm});
            skArc(sketch, "E145.filletArc", {"start": v(-67.41, -61) * mm, "mid": v(-67.03, -60.92) * mm, "end": v(-66.7, -60.7) * mm});
            skPoint(sketch, "E146.visualSharp", {"position": v(-72, -61) * mm});
            skArc(sketch, "E146.filletArc", {"start": v(-70.3, -59.3) * mm, "mid": v(-70.5, -60.38) * mm, "end": v(-69.59, -61) * mm});
            skPoint(sketch, "E147.visualSharp", {"position": v(-82, -61) * mm});
            skArc(sketch, "E147.filletArc", {"start": v(-80.3, -59.3) * mm, "mid": v(-80.5, -60.38) * mm, "end": v(-79.59, -61) * mm});
            skPoint(sketch, "E148.visualSharp", {"position": v(-77, -61) * mm});
            skArc(sketch, "E148.filletArc", {"start": v(-77.41, -61) * mm, "mid": v(-77.03, -60.92) * mm, "end": v(-76.7, -60.7) * mm});
            skPoint(sketch, "E149.visualSharp", {"position": v(-92, -61) * mm});
            skArc(sketch, "E149.filletArc", {"start": v(-90.3, -59.3) * mm, "mid": v(-90.5, -60.38) * mm, "end": v(-89.59, -61) * mm});
            skPoint(sketch, "E150.visualSharp", {"position": v(-87, -61) * mm});
            skArc(sketch, "E150.filletArc", {"start": v(-87.41, -61) * mm, "mid": v(-87.03, -60.92) * mm, "end": v(-86.7, -60.7) * mm});
            skPoint(sketch, "E151.visualSharp", {"position": v(-102, -61) * mm});
            skArc(sketch, "E151.filletArc", {"start": v(-100.3, -59.3) * mm, "mid": v(-100.5, -60.38) * mm, "end": v(-99.59, -61) * mm});
            skPoint(sketch, "E152.visualSharp", {"position": v(-112, -61) * mm});
            skArc(sketch, "E152.filletArc", {"start": v(-110.3, -59.3) * mm, "mid": v(-110.5, -60.38) * mm, "end": v(-109.59, -61) * mm});
            skPoint(sketch, "E153.visualSharp", {"position": v(-107, -61) * mm});
            skArc(sketch, "E153.filletArc", {"start": v(-107.41, -61) * mm, "mid": v(-107.03, -60.92) * mm, "end": v(-106.7, -60.7) * mm});
            skPoint(sketch, "E154.visualSharp", {"position": v(-117, -61) * mm});
            skArc(sketch, "E154.filletArc", {"start": v(-117.41, -61) * mm, "mid": v(-117.03, -60.92) * mm, "end": v(-116.7, -60.7) * mm});
            skPoint(sketch, "E155.visualSharp", {"position": v(-122, -61) * mm});
            skArc(sketch, "E155.filletArc", {"start": v(-120.3, -59.3) * mm, "mid": v(-120.5, -60.38) * mm, "end": v(-119.59, -61) * mm});
            skSolve(sketch);
        }
        {
            var Q0;
            Q0=makeQuery(id+"F7.imprint","IMPRINT",FACE,{"disambiguationData":[TD([[makeQuery(id+"F7.imprint","IMPRINT",EDGE,{"derivedFrom":sQuery(id+"F7.wireOp",EDGE,"E29.3")}),1.0]])]});
            var Q1;
            Q1=makeQuery(id+"F7.imprint","IMPRINT",FACE,{"disambiguationData":[TD([[makeQuery(id+"F7.imprint","IMPRINT",EDGE,{"derivedFrom":sQuery(id+"F7.wireOp",EDGE,"E31.2.0.0")}),-1.0]])]});
            var Q2;
            Q2=makeQuery(id+"F7.imprint","IMPRINT",FACE,{"disambiguationData":[TD([[makeQuery(id+"F7.imprint","IMPRINT",EDGE,{"derivedFrom":sQuery(id+"F7.wireOp",EDGE,"E31.4.0.0")}),-1.0]])]});
            var Q3;
            Q3=makeQuery(id+"F7.imprint","IMPRINT",FACE,{"disambiguationData":[TD([[makeQuery(id+"F7.imprint","IMPRINT",EDGE,{"derivedFrom":sQuery(id+"F7.wireOp",EDGE,"E31.6.0.0")}),-1.0]])]});
            var Q4;
            Q4=makeQuery(id+"F7.imprint","IMPRINT",FACE,{"disambiguationData":[TD([[makeQuery(id+"F7.imprint","IMPRINT",EDGE,{"derivedFrom":sQuery(id+"F7.wireOp",EDGE,"E31.8.0.0")}),-1.0]])]});
            var Q5;
            Q5=makeQuery(id+"F7.imprint","IMPRINT",FACE,{"disambiguationData":[TD([[makeQuery(id+"F7.imprint","IMPRINT",EDGE,{"derivedFrom":sQuery(id+"F7.wireOp",EDGE,"E31.10.0.0")}),-1.0]])]});
            var Q6;
            Q6=makeQuery(id+"F7.imprint","IMPRINT",FACE,{"disambiguationData":[TD([[makeQuery(id+"F7.imprint","IMPRINT",EDGE,{"derivedFrom":sQuery(id+"F7.wireOp",EDGE,"E31.12.0.0")}),-1.0]])]});
            var Q7;
            Q7=makeQuery(id+"F7.imprint","IMPRINT",FACE,{"disambiguationData":[TD([[makeQuery(id+"F7.imprint","IMPRINT",EDGE,{"derivedFrom":sQuery(id+"F7.wireOp",EDGE,"E29.2")}),1.0]])]});
            var Q8;
            Q8=makeQuery(id+"F7.imprint","IMPRINT",FACE,{"disambiguationData":[TD([[makeQuery(id+"F7.imprint","IMPRINT",EDGE,{"derivedFrom":sQuery(id+"F7.wireOp",EDGE,"E31.16.0.0")}),-1.0]])]});
            var Q9;
            Q9=makeQuery(id+"F7.imprint","IMPRINT",FACE,{"disambiguationData":[TD([[makeQuery(id+"F7.imprint","IMPRINT",EDGE,{"derivedFrom":sQuery(id+"F7.wireOp",EDGE,"E31.18.0.0")}),-1.0]])]});
            var Q10;
            Q10=makeQuery(id+"F7.imprint","IMPRINT",FACE,{"disambiguationData":[TD([[makeQuery(id+"F7.imprint","IMPRINT",EDGE,{"derivedFrom":sQuery(id+"F7.wireOp",EDGE,"E32.1.0.0")}),-1.0]])]});
            var Q11;
            Q11=makeQuery(id+"F7.imprint","IMPRINT",FACE,{"disambiguationData":[TD([[makeQuery(id+"F7.imprint","IMPRINT",EDGE,{"derivedFrom":sQuery(id+"F7.wireOp",EDGE,"E29.0")}),1.0]])]});
            var Q12;
            Q12=makeQuery(id+"F7.imprint","IMPRINT",FACE,{"disambiguationData":[TD([[makeQuery(id+"F7.imprint","IMPRINT",EDGE,{"derivedFrom":sQuery(id+"F7.wireOp",EDGE,"E49.1.0.0")}),-1.0]])]});
            var Q13;
            Q13=makeQuery(id+"F7.imprint","IMPRINT",FACE,{"disambiguationData":[TD([[makeQuery(id+"F7.imprint","IMPRINT",EDGE,{"derivedFrom":sQuery(id+"F7.wireOp",EDGE,"E49.3.0.0")}),-1.0]])]});
            var Q14;
            Q14=makeQuery(id+"F7.imprint","IMPRINT",FACE,{"disambiguationData":[TD([[makeQuery(id+"F7.imprint","IMPRINT",EDGE,{"derivedFrom":sQuery(id+"F7.wireOp",EDGE,"E49.5.0.0")}),-1.0]])]});
            var Q15;
            Q15=makeQuery(id+"F7.imprint","IMPRINT",FACE,{"disambiguationData":[TD([[makeQuery(id+"F7.imprint","IMPRINT",EDGE,{"derivedFrom":sQuery(id+"F7.wireOp",EDGE,"E49.7.0.0")}),-1.0]])]});
            var Q16;
            Q16=makeQuery(id+"F7.imprint","IMPRINT",FACE,{"disambiguationData":[TD([[makeQuery(id+"F7.imprint","IMPRINT",EDGE,{"derivedFrom":sQuery(id+"F7.wireOp",EDGE,"E49.9.0.0")}),-1.0]])]});
            var Q17;
            Q17=makeQuery(id+"F7.imprint","IMPRINT",FACE,{"disambiguationData":[TD([[makeQuery(id+"F7.imprint","IMPRINT",EDGE,{"derivedFrom":sQuery(id+"F7.wireOp",EDGE,"E49.11.0.0")}),-1.0]])]});
            var Q18;
            Q18=makeQuery(id+"F7.imprint","IMPRINT",FACE,{"disambiguationData":[TD([[makeQuery(id+"F7.imprint","IMPRINT",EDGE,{"derivedFrom":sQuery(id+"F7.wireOp",EDGE,"E29.1")}),1.0]])]});
            extrude(context, id + "F8", {"entities" : qUnion([Q0, Q1, Q2, Q3, Q4, Q5, Q6, Q7, Q8, Q9, Q10, Q11, Q12, Q13, Q14, Q15, Q16, Q17, Q18]), "operationType" : NewBodyOperationType.REMOVE, "oppositeDirection" : true, "depth" : 58.3 * mm, "offsetDistance" : 25 * mm});
        }
        {
            var Q0;
            Q0=makeQuery(id+"F2.opExtrude","CAP_EDGE",EDGE,{"disambiguationData":[OSD([sQuery(id+"F0.wireOp",EDGE,"E13.MirrorCS")])],"isStart":true});
            var Q1;
            Q1=makeQuery(id+"F2.opExtrude","CAP_EDGE",EDGE,{"disambiguationData":[OSD([sQuery(id+"F0.wireOp",EDGE,"E22.MirrorCS")])],"isStart":true});
            var Q2;
            Q2=makeQuery(id+"F3.boolean.opBoolean","MERGE",FACE,{"derivedFrom":[makeQuery(id+"F2.boolean.opBoolean","MERGE",FACE,{"derivedFrom":[makeQuery(id+"F1.opExtrude","SWEPT_FACE",FACE,{"disambiguationData":[OSD([sQuery(id+"F0.wireOp",EDGE,"E21.MirrorCS")])]}),makeQuery(id+"F2.opExtrude","SWEPT_FACE",FACE,{"disambiguationData":[OSD([sQuery(id+"F0.wireOp",EDGE,"E13.MirrorCS")])]})]}),makeQuery(id+"F3.opExtrude","SWEPT_FACE",FACE,{"disambiguationData":[OSD([sQuery(id+"F0.wireOp",EDGE,"E18.MirrorCS")])]})]});
            var Q3;
            Q3=makeQuery(id+"F2.boolean.opBoolean","MERGE",FACE,{"derivedFrom":[makeQuery(id+"F1.opExtrude","SWEPT_FACE",FACE,{"disambiguationData":[OSD([sQuery(id+"F0.wireOp",EDGE,"E19.MirrorCS")])]}),makeQuery(id+"F2.opExtrude","SWEPT_FACE",FACE,{"disambiguationData":[OSD([sQuery(id+"F0.wireOp",EDGE,"E22.MirrorCS")])]})]});
            var Q4;
            Q4=makeQuery(id+"F1.opExtrude","CAP_EDGE",EDGE,{"disambiguationData":[OSD([sQuery(id+"F0.wireOp",EDGE,"E14.MirrorCS")])],"isStart":false});
            var Q5;
            Q5=makeQuery(id+"F1.opExtrude","CAP_EDGE",EDGE,{"disambiguationData":[OSD([sQuery(id+"F0.wireOp",EDGE,"E20.MirrorCS")])],"isStart":false});
            var Q6;
            Q6=makeQuery(id+"F3.boolean.opBoolean","MERGE",FACE,{"derivedFrom":[makeQuery(id+"F2.boolean.opBoolean","MERGE",FACE,{"derivedFrom":[makeQuery(id+"F1.opExtrude","SWEPT_FACE",FACE,{"disambiguationData":[OSD([sQuery(id+"F0.wireOp",EDGE,"E4")])]}),makeQuery(id+"F2.opExtrude","SWEPT_FACE",FACE,{"disambiguationData":[OSD([sQuery(id+"F0.wireOp",EDGE,"E1")])]})]}),makeQuery(id+"F3.opExtrude","SWEPT_FACE",FACE,{"disambiguationData":[OSD([sQuery(id+"F0.wireOp",EDGE,"E7")])]})]});
            var Q7;
            Q7=makeQuery(id+"F2.boolean.opBoolean","MERGE",FACE,{"derivedFrom":[makeQuery(id+"F1.opExtrude","SWEPT_FACE",FACE,{"disambiguationData":[OSD([sQuery(id+"F0.wireOp",EDGE,"E6")])]}),makeQuery(id+"F2.opExtrude","SWEPT_FACE",FACE,{"disambiguationData":[OSD([sQuery(id+"F0.wireOp",EDGE,"E3")])]})]});
            var Q8;
            Q8=makeQuery(id+"F1.opExtrude","CAP_EDGE",EDGE,{"disambiguationData":[OSD([sQuery(id+"F0.wireOp",EDGE,"E2")])],"isStart":false});
            var Q9;
            Q9=makeQuery(id+"F1.opExtrude","CAP_EDGE",EDGE,{"disambiguationData":[OSD([sQuery(id+"F0.wireOp",EDGE,"E5")])],"isStart":false});
            var Q10;
            Q10=makeQuery(id+"F4.opExtrude","SWEPT_FACE",FACE,{"disambiguationData":[OSD([sQuery(id+"F0.wireOp",EDGE,"E25")])]});
            var Q11;
            Q11=makeQuery(id+"F4.boolean.opBoolean","MERGE",FACE,{"derivedFrom":[makeQuery(id+"F3.opExtrude","SWEPT_FACE",FACE,{"disambiguationData":[OSD([sQuery(id+"F0.wireOp",EDGE,"E12.MirrorCS"),sQuery(id+"F0.wireOp",EDGE,"E15.MirrorCS")])]}),makeQuery(id+"F4.opExtrude","SWEPT_FACE",FACE,{"disambiguationData":[OSD([sQuery(id+"F0.wireOp",EDGE,"E24")])]})]});
            var Q12;
            Q12=makeQuery(id+"F5.boolean.opBoolean","MERGE",FACE,{"derivedFrom":[makeQuery(id+"F3.opExtrude","SWEPT_FACE",FACE,{"disambiguationData":[OSD([sQuery(id+"F0.wireOp",EDGE,"E9")])]}),makeQuery(id+"F3.opExtrude","SWEPT_FACE",FACE,{"disambiguationData":[OSD([sQuery(id+"F0.wireOp",EDGE,"E16.MirrorCS")])]}),makeQuery(id+"F5.opExtrude","SWEPT_FACE",FACE,{"disambiguationData":[OSD([sQuery(id+"F0.wireOp",EDGE,"E11")])]})]});
            var Q13;
            Q13=makeQuery(id+"F4.boolean.opBoolean","MERGE",FACE,{"derivedFrom":[makeQuery(id+"F3.opExtrude","SWEPT_FACE",FACE,{"disambiguationData":[OSD([sQuery(id+"F0.wireOp",EDGE,"E0"),sQuery(id+"F0.wireOp",EDGE,"E10")])]}),makeQuery(id+"F4.opExtrude","SWEPT_FACE",FACE,{"disambiguationData":[OSD([sQuery(id+"F0.wireOp",EDGE,"E26")])]})]});
            var Q14;
            Q14=makeQuery(id+"F1.opExtrude","CAP_EDGE",EDGE,{"disambiguationData":[OSD([sQuery(id+"F0.wireOp",EDGE,"E5")])],"isStart":true});
            var Q15;
            Q15=makeQuery(id+"F1.opExtrude","CAP_EDGE",EDGE,{"disambiguationData":[OSD([sQuery(id+"F0.wireOp",EDGE,"E20.MirrorCS")])],"isStart":true});
            chamfer(context, id + "F9", {"entities" : qUnion([Q0, Q1, Q2, Q3, Q4, Q5, Q6, Q7, Q8, Q9, Q10, Q11, Q12, Q13, Q14, Q15]), "width" : 2 * mm, "tangentPropagation" : true});
        }
        {
            var Q0;
            Q0=makeQuery(id+"F4.opExtrude","SWEPT_FACE",FACE,{"disambiguationData":[OSD([sQuery(id+"F0.wireOp",EDGE,"E25")])]});
            var sketch = newSketch(context, id + "F10", { "sketchPlane" : qUnion([Q0])});
            skLineSegment(sketch, "E156.0.0", {"start": v(-148, -48) * mm, "end": v(-2, -48) * mm});
            skLineSegment(sketch, "E156.0.1", {"start": v(-2, -48) * mm, "end": v(-2, 8) * mm});
            skLineSegment(sketch, "E156.0.2", {"start": v(-2, 8) * mm, "end": v(-148, 8) * mm});
            skLineSegment(sketch, "E156.0.3", {"start": v(-148, 8) * mm, "end": v(-148, -48) * mm});
            skLineSegment(sketch, "E157", {"start": v(-75, 8) * mm, "end": v(-75, -48) * mm});
            skLineSegment(sketch, "E158.0", {"start": v(-5, 5) * mm, "end": v(-73.5, 5) * mm});
            skLineSegment(sketch, "E159.0", {"start": v(-144, -45) * mm, "end": v(-143.17, -45) * mm});
            skLineSegment(sketch, "E160.0", {"start": v(-5, -45) * mm, "end": v(-5, 5) * mm});
            skLineSegment(sketch, "E161.0", {"start": v(-145, -1.01) * mm, "end": v(-145, -2.42) * mm});
            skLineSegment(sketch, "E162.trimOffspring", {"start": v(-81.17, 5) * mm, "end": v(-82.58, 5) * mm});
            skLineSegment(sketch, "E163.trimOffspring", {"start": v(-73.5, -45) * mm, "end": v(-5, -45) * mm});
            skLineSegment(sketch, "E164", {"start": v(-143.3, -42.7) * mm, "end": v(-142.54, -43.46) * mm});
            skLineSegment(sketch, "E165.0", {"start": v(-144.7, -37.05) * mm, "end": v(-137.05, -44.7) * mm});
            skLineSegment(sketch, "E166.1.0.0", {"start": v(-143.3, -34.23) * mm, "end": v(-134.23, -43.3) * mm});
            skLineSegment(sketch, "E166.1.0.1", {"start": v(-144.7, -28.57) * mm, "end": v(-128.57, -44.7) * mm});
            skLineSegment(sketch, "E166.2.0.0", {"start": v(-143.3, -25.75) * mm, "end": v(-125.75, -43.3) * mm});
            skLineSegment(sketch, "E166.2.0.1", {"start": v(-145, -19.8) * mm, "end": v(-120.1, -44.7) * mm});
            skLineSegment(sketch, "E166.3.0.0", {"start": v(-143.3, -17.27) * mm, "end": v(-117.27, -43.3) * mm});
            skLineSegment(sketch, "E166.3.0.1", {"start": v(-144.7, -11.61) * mm, "end": v(-111.61, -44.7) * mm});
            skLineSegment(sketch, "E166.4.0.0", {"start": v(-143.3, -8.79) * mm, "end": v(-108.79, -43.3) * mm});
            skLineSegment(sketch, "E166.4.0.1", {"start": v(-144.7, -3.13) * mm, "end": v(-103.13, -44.7) * mm});
            skLineSegment(sketch, "E166.5.0.0", {"start": v(-143.3, -0.3) * mm, "end": v(-100.3, -43.3) * mm});
            skLineSegment(sketch, "E166.5.0.1", {"start": v(-142.65, 3.3) * mm, "end": v(-94.65, -44.7) * mm});
            skLineSegment(sketch, "E166.6.0.0", {"start": v(-139.83, 4.7) * mm, "end": v(-91.83, -43.3) * mm});
            skLineSegment(sketch, "E166.6.0.1", {"start": v(-134.17, 3.3) * mm, "end": v(-86.17, -44.7) * mm});
            skLineSegment(sketch, "E166.7.0.0", {"start": v(-131.35, 4.7) * mm, "end": v(-83.35, -43.3) * mm});
            skLineSegment(sketch, "E166.7.0.1", {"start": v(-125.7, 3.3) * mm, "end": v(-77.7, -44.7) * mm});
            skLineSegment(sketch, "E166.direction1", {"start": v(-136.76, -45) * mm, "end": v(-132.52, -45) * mm, "construction": true});
            skLineSegment(sketch, "E167.0", {"start": v(-76.5, 0.33) * mm, "end": v(-76.5, -1.08) * mm});
            skLineSegment(sketch, "E168.0", {"start": v(-73.5, 5) * mm, "end": v(-73.5, -45) * mm});
            skLineSegment(sketch, "E169.MirrorCS", {"start": v(-122.86, 4.7) * mm, "end": v(-76.8, -41.36) * mm});
            skLineSegment(sketch, "E170.MirrorCS", {"start": v(-117.21, 3.3) * mm, "end": v(-78.2, -35.71) * mm});
            skLineSegment(sketch, "E171.MirrorCS", {"start": v(-114.38, 4.7) * mm, "end": v(-76.8, -32.88) * mm});
            skLineSegment(sketch, "E172.MirrorCS", {"start": v(-108.73, 3.3) * mm, "end": v(-78.2, -27.23) * mm});
            skLineSegment(sketch, "E173.MirrorCS", {"start": v(-105.9, 4.7) * mm, "end": v(-76.8, -24.4) * mm});
            skLineSegment(sketch, "E174.MirrorCS", {"start": v(-100.25, 3.3) * mm, "end": v(-78.72, -18.24) * mm});
            skLineSegment(sketch, "E175.MirrorCS", {"start": v(-97.42, 4.7) * mm, "end": v(-76.8, -15.92) * mm});
            skLineSegment(sketch, "E176.MirrorCS", {"start": v(-89.23, 5) * mm, "end": v(-77.4, -6.84) * mm});
            skLineSegment(sketch, "E177.MirrorCS", {"start": v(-91.77, 3.3) * mm, "end": v(-78.38, -10.1) * mm});
            skLineSegment(sketch, "E178.MirrorCS", {"start": v(-88.94, 4.7) * mm, "end": v(-76.8, -7.44) * mm});
            skLineSegment(sketch, "E179.MirrorCS", {"start": v(-83.3, 3.3) * mm, "end": v(-78.2, -1.8) * mm});
            skLineSegment(sketch, "E180.MirrorCS", {"start": v(-80.46, 4.7) * mm, "end": v(-76.8, 1.04) * mm});
            skPoint(sketch, "E181.orphan", {"position": v(-77.4, 1.64) * mm});
            skPoint(sketch, "E182.orphan", {"position": v(-77.4, -2.6) * mm});
            skPoint(sketch, "E183.orphan", {"position": v(-77.4, -6.84) * mm});
            skPoint(sketch, "E184.orphan", {"position": v(-77.4, -11.08) * mm});
            skPoint(sketch, "E185.orphan", {"position": v(-77.4, -15.32) * mm});
            skPoint(sketch, "E186.orphan", {"position": v(-77.4, -19.56) * mm});
            skPoint(sketch, "E187.orphan", {"position": v(-77.4, -23.8) * mm});
            skPoint(sketch, "E188.orphan", {"position": v(-77.4, -28.04) * mm});
            skPoint(sketch, "E189.orphan", {"position": v(-77.4, -32.28) * mm});
            skPoint(sketch, "E190.orphan", {"position": v(-77.4, -36.52) * mm});
            skPoint(sketch, "E191.orphan", {"position": v(-77.4, -40.76) * mm});
            skLineSegment(sketch, "E192.trimOffspring", {"start": v(-145, -43.41) * mm, "end": v(-145, -44) * mm});
            skLineSegment(sketch, "E193.trimOffspring", {"start": v(-145, -34.93) * mm, "end": v(-145, -36.34) * mm});
            skLineSegment(sketch, "E194.trimOffspring", {"start": v(-145, -26.45) * mm, "end": v(-145, -27.86) * mm});
            skLineSegment(sketch, "E195.trimOffspring", {"start": v(-127.86, -45) * mm, "end": v(-126.45, -45) * mm});
            skLineSegment(sketch, "E196.trimOffspring", {"start": v(-119.38, -45) * mm, "end": v(-117.97, -45) * mm});
            skLineSegment(sketch, "E197.trimOffspring", {"start": v(-136.34, -45) * mm, "end": v(-134.93, -45) * mm});
            skLineSegment(sketch, "E198.trimOffspring", {"start": v(-110.9, -45) * mm, "end": v(-109.5, -45) * mm});
            skLineSegment(sketch, "E199.trimOffspring", {"start": v(-102.42, -45) * mm, "end": v(-101.01, -45) * mm});
            skLineSegment(sketch, "E200.trimOffspring", {"start": v(-145, -17.97) * mm, "end": v(-145, -19.8) * mm});
            skLineSegment(sketch, "E201.trimOffspring", {"start": v(-145, -9.5) * mm, "end": v(-145, -10.9) * mm});
            skLineSegment(sketch, "E202.trimOffspring", {"start": v(-140.53, 5) * mm, "end": v(-141.94, 5) * mm});
            skLineSegment(sketch, "E203.trimOffspring", {"start": v(-132.05, 5) * mm, "end": v(-133.46, 5) * mm});
            skLineSegment(sketch, "E204.trimOffspring", {"start": v(-123.57, 5) * mm, "end": v(-124.98, 5) * mm});
            skLineSegment(sketch, "E205.trimOffspring", {"start": v(-93.94, -45) * mm, "end": v(-92.53, -45) * mm});
            skLineSegment(sketch, "E206.trimOffspring", {"start": v(-85.46, -45) * mm, "end": v(-84.05, -45) * mm});
            skLineSegment(sketch, "E207.trimOffspring", {"start": v(-77, -45) * mm, "end": v(-76.98, -45) * mm});
            skLineSegment(sketch, "E208.trimOffspring", {"start": v(-76.5, -42.07) * mm, "end": v(-76.5, -44.5) * mm});
            skLineSegment(sketch, "E209.trimOffspring", {"start": v(-76.5, -33.59) * mm, "end": v(-76.5, -35) * mm});
            skLineSegment(sketch, "E210.trimOffspring", {"start": v(-76.5, -25.1) * mm, "end": v(-76.5, -26.52) * mm});
            skLineSegment(sketch, "E211.trimOffspring", {"start": v(-76.5, -16.63) * mm, "end": v(-76.5, -17.32) * mm});
            skLineSegment(sketch, "E212.trimOffspring", {"start": v(-76.5, -8.15) * mm, "end": v(-76.5, -9.32) * mm});
            skLineSegment(sketch, "E213.trimOffspring", {"start": v(-115.09, 5) * mm, "end": v(-116.5, 5) * mm});
            skLineSegment(sketch, "E214.trimOffspring", {"start": v(-106.6, 5) * mm, "end": v(-108.02, 5) * mm});
            skLineSegment(sketch, "E215.trimOffspring", {"start": v(-98.13, 5) * mm, "end": v(-99.54, 5) * mm});
            skLineSegment(sketch, "E216.trimOffspring", {"start": v(-89.65, 5) * mm, "end": v(-91.06, 5) * mm});
            skPoint(sketch, "E217.visualSharp", {"position": v(-145, 1.4) * mm});
            skArc(sketch, "E217.filletArc", {"start": v(-143.3, -0.3) * mm, "mid": v(-144.38, -0.1) * mm, "end": v(-145, -1.01) * mm});
            skPoint(sketch, "E218.visualSharp", {"position": v(-145, -2.84) * mm});
            skArc(sketch, "E218.filletArc", {"start": v(-145, -2.42) * mm, "mid": v(-144.92, -2.8) * mm, "end": v(-144.7, -3.13) * mm});
            skPoint(sketch, "E219.visualSharp", {"position": v(-144.36, 5) * mm});
            skArc(sketch, "E219.filletArc", {"start": v(-141.94, 5) * mm, "mid": v(-142.87, 4.38) * mm, "end": v(-142.65, 3.3) * mm});
            skPoint(sketch, "E220.visualSharp", {"position": v(-140.12, 5) * mm});
            skArc(sketch, "E220.filletArc", {"start": v(-139.83, 4.7) * mm, "mid": v(-140.15, 4.92) * mm, "end": v(-140.53, 5) * mm});
            skPoint(sketch, "E221.visualSharp", {"position": v(-135.88, 5) * mm});
            skArc(sketch, "E221.filletArc", {"start": v(-133.46, 5) * mm, "mid": v(-134.39, 4.38) * mm, "end": v(-134.17, 3.3) * mm});
            skPoint(sketch, "E222.visualSharp", {"position": v(-131.64, 5) * mm});
            skArc(sketch, "E222.filletArc", {"start": v(-131.35, 4.7) * mm, "mid": v(-131.67, 4.92) * mm, "end": v(-132.05, 5) * mm});
            skPoint(sketch, "E223.visualSharp", {"position": v(-127.4, 5) * mm});
            skArc(sketch, "E223.filletArc", {"start": v(-124.98, 5) * mm, "mid": v(-125.9, 4.38) * mm, "end": v(-125.7, 3.3) * mm});
            skPoint(sketch, "E224.visualSharp", {"position": v(-123.15, 5) * mm});
            skArc(sketch, "E224.filletArc", {"start": v(-122.86, 4.7) * mm, "mid": v(-123.19, 4.92) * mm, "end": v(-123.57, 5) * mm});
            skPoint(sketch, "E225.visualSharp", {"position": v(-118.92, 5) * mm});
            skArc(sketch, "E225.filletArc", {"start": v(-116.5, 5) * mm, "mid": v(-117.43, 4.38) * mm, "end": v(-117.21, 3.3) * mm});
            skPoint(sketch, "E226.visualSharp", {"position": v(-114.67, 5) * mm});
            skArc(sketch, "E226.filletArc", {"start": v(-114.38, 4.7) * mm, "mid": v(-114.7, 4.92) * mm, "end": v(-115.09, 5) * mm});
            skPoint(sketch, "E227.visualSharp", {"position": v(-110.44, 5) * mm});
            skArc(sketch, "E227.filletArc", {"start": v(-108.02, 5) * mm, "mid": v(-108.95, 4.38) * mm, "end": v(-108.73, 3.3) * mm});
            skPoint(sketch, "E228.visualSharp", {"position": v(-106.2, 5) * mm});
            skArc(sketch, "E228.filletArc", {"start": v(-105.9, 4.7) * mm, "mid": v(-106.23, 4.92) * mm, "end": v(-106.6, 5) * mm});
            skPoint(sketch, "E229.visualSharp", {"position": v(-101.96, 5) * mm});
            skArc(sketch, "E229.filletArc", {"start": v(-99.54, 5) * mm, "mid": v(-100.47, 4.38) * mm, "end": v(-100.25, 3.3) * mm});
            skPoint(sketch, "E230.visualSharp", {"position": v(-97.71, 5) * mm});
            skArc(sketch, "E230.filletArc", {"start": v(-97.42, 4.7) * mm, "mid": v(-97.75, 4.92) * mm, "end": v(-98.13, 5) * mm});
            skPoint(sketch, "E231.visualSharp", {"position": v(-93.48, 5) * mm});
            skArc(sketch, "E231.filletArc", {"start": v(-91.06, 5) * mm, "mid": v(-91.99, 4.38) * mm, "end": v(-91.77, 3.3) * mm});
            skPoint(sketch, "E232.visualSharp", {"position": v(-89.23, 5) * mm});
            skArc(sketch, "E232.filletArc", {"start": v(-88.94, 4.7) * mm, "mid": v(-89.27, 4.92) * mm, "end": v(-89.65, 5) * mm});
            skPoint(sketch, "E233.visualSharp", {"position": v(-85, 5) * mm});
            skArc(sketch, "E233.filletArc", {"start": v(-82.58, 5) * mm, "mid": v(-83.5, 4.38) * mm, "end": v(-83.3, 3.3) * mm});
            skPoint(sketch, "E234.visualSharp", {"position": v(-80.75, 5) * mm});
            skArc(sketch, "E234.filletArc", {"start": v(-80.46, 4.7) * mm, "mid": v(-80.79, 4.92) * mm, "end": v(-81.17, 5) * mm});
            skPoint(sketch, "E235.visualSharp", {"position": v(-76.5, -3.5) * mm});
            skArc(sketch, "E235.filletArc", {"start": v(-78.2, -1.8) * mm, "mid": v(-77.12, -2) * mm, "end": v(-76.5, -1.08) * mm});
            skPoint(sketch, "E236.visualSharp", {"position": v(-76.5, 0.75) * mm});
            skArc(sketch, "E236.filletArc", {"start": v(-76.5, 0.33) * mm, "mid": v(-76.58, 0.71) * mm, "end": v(-76.8, 1.04) * mm});
            skPoint(sketch, "E237.visualSharp", {"position": v(-76.5, -7.73) * mm});
            skArc(sketch, "E237.filletArc", {"start": v(-76.5, -8.15) * mm, "mid": v(-76.58, -7.77) * mm, "end": v(-76.8, -7.44) * mm});
            skPoint(sketch, "E238.visualSharp", {"position": v(-76.5, -11.98) * mm});
            skArc(sketch, "E238.filletArc", {"start": v(-78.38, -10.1) * mm, "mid": v(-77.18, -10.34) * mm, "end": v(-76.5, -9.32) * mm});
            skPoint(sketch, "E239.visualSharp", {"position": v(-76.5, -16.21) * mm});
            skArc(sketch, "E239.filletArc", {"start": v(-76.5, -16.63) * mm, "mid": v(-76.58, -16.25) * mm, "end": v(-76.8, -15.92) * mm});
            skPoint(sketch, "E240.visualSharp", {"position": v(-76.5, -20.46) * mm});
            skArc(sketch, "E240.filletArc", {"start": v(-78.72, -18.24) * mm, "mid": v(-77.3, -18.52) * mm, "end": v(-76.5, -17.32) * mm});
            skPoint(sketch, "E241.visualSharp", {"position": v(-76.5, -24.7) * mm});
            skArc(sketch, "E241.filletArc", {"start": v(-76.5, -25.1) * mm, "mid": v(-76.58, -24.73) * mm, "end": v(-76.8, -24.4) * mm});
            skPoint(sketch, "E242.visualSharp", {"position": v(-76.5, -28.94) * mm});
            skArc(sketch, "E242.filletArc", {"start": v(-78.2, -27.23) * mm, "mid": v(-77.12, -27.45) * mm, "end": v(-76.5, -26.52) * mm});
            skPoint(sketch, "E243.visualSharp", {"position": v(-76.5, -33.17) * mm});
            skArc(sketch, "E243.filletArc", {"start": v(-76.5, -33.59) * mm, "mid": v(-76.58, -33.2) * mm, "end": v(-76.8, -32.88) * mm});
            skPoint(sketch, "E244.visualSharp", {"position": v(-76.5, -41.65) * mm});
            skArc(sketch, "E244.filletArc", {"start": v(-76.5, -42.07) * mm, "mid": v(-76.58, -41.69) * mm, "end": v(-76.8, -41.36) * mm});
            skPoint(sketch, "E245.visualSharp", {"position": v(-77.4, -45) * mm});
            skArc(sketch, "E245.filletArc", {"start": v(-77.7, -44.7) * mm, "mid": v(-77.37, -44.92) * mm, "end": v(-76.98, -45) * mm});
            skPoint(sketch, "E246.visualSharp", {"position": v(-81.64, -45) * mm});
            skArc(sketch, "E246.filletArc", {"start": v(-84.05, -45) * mm, "mid": v(-83.13, -44.38) * mm, "end": v(-83.35, -43.3) * mm});
            skPoint(sketch, "E247.visualSharp", {"position": v(-85.88, -45) * mm});
            skArc(sketch, "E247.filletArc", {"start": v(-86.17, -44.7) * mm, "mid": v(-85.85, -44.92) * mm, "end": v(-85.46, -45) * mm});
            skPoint(sketch, "E248.visualSharp", {"position": v(-76.5, -37.42) * mm});
            skArc(sketch, "E248.filletArc", {"start": v(-78.2, -35.71) * mm, "mid": v(-77.12, -35.93) * mm, "end": v(-76.5, -35) * mm});
            skPoint(sketch, "E249.visualSharp", {"position": v(-76.5, -45) * mm});
            skArc(sketch, "E249.filletArc", {"start": v(-77, -45) * mm, "mid": v(-76.65, -44.85) * mm, "end": v(-76.5, -44.5) * mm});
            skPoint(sketch, "E250.visualSharp", {"position": v(-90.12, -45) * mm});
            skArc(sketch, "E250.filletArc", {"start": v(-92.53, -45) * mm, "mid": v(-91.61, -44.38) * mm, "end": v(-91.83, -43.3) * mm});
            skPoint(sketch, "E251.visualSharp", {"position": v(-94.36, -45) * mm});
            skArc(sketch, "E251.filletArc", {"start": v(-94.65, -44.7) * mm, "mid": v(-94.33, -44.92) * mm, "end": v(-93.94, -45) * mm});
            skPoint(sketch, "E252.visualSharp", {"position": v(-98.6, -45) * mm});
            skArc(sketch, "E252.filletArc", {"start": v(-101.01, -45) * mm, "mid": v(-100.1, -44.38) * mm, "end": v(-100.3, -43.3) * mm});
            skPoint(sketch, "E253.visualSharp", {"position": v(-102.84, -45) * mm});
            skArc(sketch, "E253.filletArc", {"start": v(-103.13, -44.7) * mm, "mid": v(-102.8, -44.92) * mm, "end": v(-102.42, -45) * mm});
            skPoint(sketch, "E254.visualSharp", {"position": v(-111.32, -45) * mm});
            skArc(sketch, "E254.filletArc", {"start": v(-111.61, -44.7) * mm, "mid": v(-111.29, -44.92) * mm, "end": v(-110.9, -45) * mm});
            skPoint(sketch, "E255.visualSharp", {"position": v(-107.08, -45) * mm});
            skArc(sketch, "E255.filletArc", {"start": v(-109.5, -45) * mm, "mid": v(-108.57, -44.38) * mm, "end": v(-108.79, -43.3) * mm});
            skPoint(sketch, "E256.visualSharp", {"position": v(-115.56, -45) * mm});
            skArc(sketch, "E256.filletArc", {"start": v(-117.97, -45) * mm, "mid": v(-117.05, -44.38) * mm, "end": v(-117.27, -43.3) * mm});
            skPoint(sketch, "E257.visualSharp", {"position": v(-119.8, -45) * mm});
            skArc(sketch, "E257.filletArc", {"start": v(-120.1, -44.7) * mm, "mid": v(-119.77, -44.92) * mm, "end": v(-119.38, -45) * mm});
            skPoint(sketch, "E258.visualSharp", {"position": v(-124.04, -45) * mm});
            skArc(sketch, "E258.filletArc", {"start": v(-126.45, -45) * mm, "mid": v(-125.53, -44.38) * mm, "end": v(-125.75, -43.3) * mm});
            skPoint(sketch, "E259.visualSharp", {"position": v(-128.28, -45) * mm});
            skArc(sketch, "E259.filletArc", {"start": v(-128.57, -44.7) * mm, "mid": v(-128.25, -44.92) * mm, "end": v(-127.86, -45) * mm});
            skPoint(sketch, "E260.visualSharp", {"position": v(-132.52, -45) * mm});
            skArc(sketch, "E260.filletArc", {"start": v(-134.93, -45) * mm, "mid": v(-134.01, -44.38) * mm, "end": v(-134.23, -43.3) * mm});
            skPoint(sketch, "E261.visualSharp", {"position": v(-136.76, -45) * mm});
            skArc(sketch, "E261.filletArc", {"start": v(-137.05, -44.7) * mm, "mid": v(-136.73, -44.92) * mm, "end": v(-136.34, -45) * mm});
            skPoint(sketch, "E262.visualSharp", {"position": v(-141, -45) * mm});
            skArc(sketch, "E262.filletArc", {"start": v(-143.17, -45) * mm, "mid": v(-142.34, -44.44) * mm, "end": v(-142.54, -43.46) * mm});
            skPoint(sketch, "E263.visualSharp", {"position": v(-145, -41) * mm});
            skArc(sketch, "E263.filletArc", {"start": v(-143.3, -42.7) * mm, "mid": v(-144.38, -42.5) * mm, "end": v(-145, -43.41) * mm});
            skPoint(sketch, "E264.visualSharp", {"position": v(-145, -45) * mm});
            skArc(sketch, "E264.filletArc", {"start": v(-145, -44) * mm, "mid": v(-144.7, -44.7) * mm, "end": v(-144, -45) * mm});
            skPoint(sketch, "E265.visualSharp", {"position": v(-145, -36.76) * mm});
            skArc(sketch, "E265.filletArc", {"start": v(-145, -36.34) * mm, "mid": v(-144.92, -36.73) * mm, "end": v(-144.7, -37.05) * mm});
            skPoint(sketch, "E266.visualSharp", {"position": v(-145, -32.52) * mm});
            skArc(sketch, "E266.filletArc", {"start": v(-143.3, -34.23) * mm, "mid": v(-144.38, -34.01) * mm, "end": v(-145, -34.93) * mm});
            skPoint(sketch, "E267.visualSharp", {"position": v(-145, -28.28) * mm});
            skArc(sketch, "E267.filletArc", {"start": v(-145, -27.86) * mm, "mid": v(-144.92, -28.25) * mm, "end": v(-144.7, -28.57) * mm});
            skPoint(sketch, "E268.visualSharp", {"position": v(-145, -24.04) * mm});
            skArc(sketch, "E268.filletArc", {"start": v(-143.3, -25.75) * mm, "mid": v(-144.38, -25.53) * mm, "end": v(-145, -26.45) * mm});
            skPoint(sketch, "E269.visualSharp", {"position": v(-145, -15.56) * mm});
            skArc(sketch, "E269.filletArc", {"start": v(-143.3, -17.27) * mm, "mid": v(-144.38, -17.05) * mm, "end": v(-145, -17.97) * mm});
            skPoint(sketch, "E270.visualSharp", {"position": v(-145, -11.32) * mm});
            skArc(sketch, "E270.filletArc", {"start": v(-145, -10.9) * mm, "mid": v(-144.92, -11.29) * mm, "end": v(-144.7, -11.61) * mm});
            skPoint(sketch, "E271.visualSharp", {"position": v(-145, -7.08) * mm});
            skArc(sketch, "E271.filletArc", {"start": v(-143.3, -8.79) * mm, "mid": v(-144.38, -8.57) * mm, "end": v(-145, -9.5) * mm});
            skArc(sketch, "E272.MirrorCS", {"start": v(-73, -45) * mm, "mid": v(-73.35, -44.85) * mm, "end": v(-73.5, -44.5) * mm});
            skLineSegment(sketch, "E273.MirrorCS", {"start": v(-73, -45) * mm, "end": v(-73.02, -45) * mm});
            skArc(sketch, "E274.MirrorCS", {"start": v(-72.3, -44.7) * mm, "mid": v(-72.63, -44.92) * mm, "end": v(-73.02, -45) * mm});
            skArc(sketch, "E275.MirrorCS", {"start": v(-73.5, -8.15) * mm, "mid": v(-73.42, -7.77) * mm, "end": v(-73.2, -7.44) * mm});
            skArc(sketch, "E276.MirrorCS", {"start": v(-73.5, -42.07) * mm, "mid": v(-73.42, -41.69) * mm, "end": v(-73.2, -41.36) * mm});
            skArc(sketch, "E277.MirrorCS", {"start": v(-73.5, 0.33) * mm, "mid": v(-73.42, 0.71) * mm, "end": v(-73.2, 1.04) * mm});
            skArc(sketch, "E278.MirrorCS", {"start": v(-73.5, -16.63) * mm, "mid": v(-73.42, -16.25) * mm, "end": v(-73.2, -15.92) * mm});
            skLineSegment(sketch, "E279.MirrorCS", {"start": v(-73.5, -16.63) * mm, "end": v(-73.5, -17.32) * mm});
            skLineSegment(sketch, "E280.MirrorCS", {"start": v(-73.5, -42.07) * mm, "end": v(-73.5, -44.5) * mm});
            skArc(sketch, "E281.MirrorCS", {"start": v(-29.9, -44.7) * mm, "mid": v(-30.23, -44.92) * mm, "end": v(-30.62, -45) * mm});
            skArc(sketch, "E282.MirrorCS", {"start": v(-73.5, -25.1) * mm, "mid": v(-73.42, -24.73) * mm, "end": v(-73.2, -24.4) * mm});
            skLineSegment(sketch, "E283.MirrorCS", {"start": v(-73.5, -33.59) * mm, "end": v(-73.5, -35) * mm});
            skLineSegment(sketch, "E284.MirrorCS", {"start": v(-73.5, -25.1) * mm, "end": v(-73.5, -26.52) * mm});
            skLineSegment(sketch, "E285.MirrorCS", {"start": v(-73.5, 0.33) * mm, "end": v(-73.5, -1.08) * mm});
            skArc(sketch, "E286.MirrorCS", {"start": v(-35.62, 4.7) * mm, "mid": v(-35.3, 4.92) * mm, "end": v(-34.91, 5) * mm});
            skArc(sketch, "E287.MirrorCS", {"start": v(-73.5, -33.59) * mm, "mid": v(-73.42, -33.2) * mm, "end": v(-73.2, -32.88) * mm});
            skArc(sketch, "E288.MirrorCS", {"start": v(-21.43, -44.7) * mm, "mid": v(-21.75, -44.92) * mm, "end": v(-22.14, -45) * mm});
            skArc(sketch, "E289.MirrorCS", {"start": v(-46.87, -44.7) * mm, "mid": v(-47.2, -44.92) * mm, "end": v(-47.58, -45) * mm});
            skArc(sketch, "E290.MirrorCS", {"start": v(-38.39, -44.7) * mm, "mid": v(-38.71, -44.92) * mm, "end": v(-39.1, -45) * mm});
            skArc(sketch, "E291.MirrorCS", {"start": v(-5, -10.9) * mm, "mid": v(-5.08, -11.29) * mm, "end": v(-5.3, -11.61) * mm});
            skArc(sketch, "E292.MirrorCS", {"start": v(-18.65, 4.7) * mm, "mid": v(-18.33, 4.92) * mm, "end": v(-17.95, 5) * mm});
            skLineSegment(sketch, "E293.MirrorCS", {"start": v(-6, -45) * mm, "end": v(-6.83, -45) * mm});
            skArc(sketch, "E294.MirrorCS", {"start": v(-69.54, 4.7) * mm, "mid": v(-69.21, 4.92) * mm, "end": v(-68.83, 5) * mm});
            skArc(sketch, "E295.MirrorCS", {"start": v(-5, -44) * mm, "mid": v(-5.3, -44.7) * mm, "end": v(-6, -45) * mm});
            skArc(sketch, "E296.MirrorCS", {"start": v(-5, -2.42) * mm, "mid": v(-5.08, -2.8) * mm, "end": v(-5.3, -3.13) * mm});
            skArc(sketch, "E297.MirrorCS", {"start": v(-61.06, 4.7) * mm, "mid": v(-60.73, 4.92) * mm, "end": v(-60.35, 5) * mm});
            skArc(sketch, "E298.MirrorCS", {"start": v(-63.83, -44.7) * mm, "mid": v(-64.15, -44.92) * mm, "end": v(-64.54, -45) * mm});
            skArc(sketch, "E299.MirrorCS", {"start": v(-12.95, -44.7) * mm, "mid": v(-13.27, -44.92) * mm, "end": v(-13.66, -45) * mm});
            skLineSegment(sketch, "E300.MirrorCS", {"start": v(-26.43, 5) * mm, "end": v(-25.02, 5) * mm});
            skArc(sketch, "E301.MirrorCS", {"start": v(-10.17, 4.7) * mm, "mid": v(-9.85, 4.92) * mm, "end": v(-9.47, 5) * mm});
            skArc(sketch, "E302.MirrorCS", {"start": v(-58.94, 5) * mm, "mid": v(-58.01, 4.38) * mm, "end": v(-58.23, 3.3) * mm});
            skArc(sketch, "E303.MirrorCS", {"start": v(-52.58, 4.7) * mm, "mid": v(-52.25, 4.92) * mm, "end": v(-51.87, 5) * mm});
            skArc(sketch, "E304.MirrorCS", {"start": v(-27.14, 4.7) * mm, "mid": v(-26.81, 4.92) * mm, "end": v(-26.43, 5) * mm});
            skLineSegment(sketch, "E305.MirrorCS", {"start": v(-30.62, -45) * mm, "end": v(-32.03, -45) * mm});
            skArc(sketch, "E306.MirrorCS", {"start": v(-32.03, -45) * mm, "mid": v(-32.95, -44.38) * mm, "end": v(-32.73, -43.3) * mm});
            skLineSegment(sketch, "E307.MirrorCS", {"start": v(-5, -43.41) * mm, "end": v(-5, -44) * mm});
            skArc(sketch, "E308.MirrorCS", {"start": v(-5, -27.86) * mm, "mid": v(-5.08, -28.25) * mm, "end": v(-5.3, -28.57) * mm});
            skArc(sketch, "E309.MirrorCS", {"start": v(-55.35, -44.7) * mm, "mid": v(-55.67, -44.92) * mm, "end": v(-56.06, -45) * mm});
            skArc(sketch, "E310.MirrorCS", {"start": v(-6.83, -45) * mm, "mid": v(-7.66, -44.44) * mm, "end": v(-7.46, -43.46) * mm});
            skArc(sketch, "E311.MirrorCS", {"start": v(-5, -36.34) * mm, "mid": v(-5.08, -36.73) * mm, "end": v(-5.3, -37.05) * mm});
            skLineSegment(sketch, "E312.MirrorCS", {"start": v(-64.54, -45) * mm, "end": v(-65.95, -45) * mm});
            skArc(sketch, "E313.MirrorCS", {"start": v(-44.1, 4.7) * mm, "mid": v(-43.77, 4.92) * mm, "end": v(-43.4, 5) * mm});
            skLineSegment(sketch, "E314.MirrorCS", {"start": v(-73.5, -8.15) * mm, "end": v(-73.5, -9.32) * mm});
            skArc(sketch, "E315.MirrorCS", {"start": v(-33.5, 5) * mm, "mid": v(-32.57, 4.38) * mm, "end": v(-32.79, 3.3) * mm});
            skArc(sketch, "E316.MirrorCS", {"start": v(-15.07, -45) * mm, "mid": v(-15.99, -44.38) * mm, "end": v(-15.77, -43.3) * mm});
            skLineSegment(sketch, "E317.MirrorCS", {"start": v(-13.24, -45) * mm, "end": v(-17.48, -45) * mm, "construction": true});
            skLineSegment(sketch, "E318.MirrorCS", {"start": v(-5, -34.93) * mm, "end": v(-5, -36.34) * mm});
            skLineSegment(sketch, "E319.MirrorCS", {"start": v(-5, -26.45) * mm, "end": v(-5, -27.86) * mm});
            skArc(sketch, "E320.MirrorCS", {"start": v(-23.55, -45) * mm, "mid": v(-24.47, -44.38) * mm, "end": v(-24.25, -43.3) * mm});
            skArc(sketch, "E321.MirrorCS", {"start": v(-71.8, -27.23) * mm, "mid": v(-72.88, -27.45) * mm, "end": v(-73.5, -26.52) * mm});
            skArc(sketch, "E322.MirrorCS", {"start": v(-6.7, -8.79) * mm, "mid": v(-5.62, -8.57) * mm, "end": v(-5, -9.5) * mm});
            skArc(sketch, "E323.MirrorCS", {"start": v(-67.42, 5) * mm, "mid": v(-66.5, 4.38) * mm, "end": v(-66.7, 3.3) * mm});
            skArc(sketch, "E324.MirrorCS", {"start": v(-16.54, 5) * mm, "mid": v(-15.61, 4.38) * mm, "end": v(-15.83, 3.3) * mm});
            skArc(sketch, "E325.MirrorCS", {"start": v(-6.7, -17.27) * mm, "mid": v(-5.62, -17.05) * mm, "end": v(-5, -17.97) * mm});
            skLineSegment(sketch, "E326.MirrorCS", {"start": v(-56.06, -45) * mm, "end": v(-57.47, -45) * mm});
            skArc(sketch, "E327.MirrorCS", {"start": v(-71.62, -10.1) * mm, "mid": v(-72.82, -10.34) * mm, "end": v(-73.5, -9.32) * mm});
            skLineSegment(sketch, "E328.MirrorCS", {"start": v(-17.95, 5) * mm, "end": v(-16.54, 5) * mm});
            skArc(sketch, "E329.MirrorCS", {"start": v(-8.06, 5) * mm, "mid": v(-7.13, 4.38) * mm, "end": v(-7.35, 3.3) * mm});
            skArc(sketch, "E330.MirrorCS", {"start": v(-71.8, -35.71) * mm, "mid": v(-72.88, -35.93) * mm, "end": v(-73.5, -35) * mm});
            skLineSegment(sketch, "E331.MirrorCS", {"start": v(-9.47, 5) * mm, "end": v(-8.06, 5) * mm});
            skArc(sketch, "E332.MirrorCS", {"start": v(-71.8, -1.8) * mm, "mid": v(-72.88, -2) * mm, "end": v(-73.5, -1.08) * mm});
            skLineSegment(sketch, "E333.MirrorCS", {"start": v(-5, -17.97) * mm, "end": v(-5, -19.8) * mm});
            skArc(sketch, "E334.MirrorCS", {"start": v(-57.47, -45) * mm, "mid": v(-58.39, -44.38) * mm, "end": v(-58.17, -43.3) * mm});
            skArc(sketch, "E335.MirrorCS", {"start": v(-6.7, -34.23) * mm, "mid": v(-5.62, -34.01) * mm, "end": v(-5, -34.93) * mm});
            skLineSegment(sketch, "E336.MirrorCS", {"start": v(-60.35, 5) * mm, "end": v(-58.94, 5) * mm});
            skLineSegment(sketch, "E337.MirrorCS", {"start": v(-47.58, -45) * mm, "end": v(-48.99, -45) * mm});
            skArc(sketch, "E338.MirrorCS", {"start": v(-48.99, -45) * mm, "mid": v(-49.9, -44.38) * mm, "end": v(-49.7, -43.3) * mm});
            skLineSegment(sketch, "E339.MirrorCS", {"start": v(-34.91, 5) * mm, "end": v(-33.5, 5) * mm});
            skLineSegment(sketch, "E340.MirrorCS", {"start": v(-13.66, -45) * mm, "end": v(-15.07, -45) * mm});
            skArc(sketch, "E341.MirrorCS", {"start": v(-50.46, 5) * mm, "mid": v(-49.53, 4.38) * mm, "end": v(-49.75, 3.3) * mm});
            skLineSegment(sketch, "E342.MirrorCS", {"start": v(-5, -1.01) * mm, "end": v(-5, -2.42) * mm});
            skLineSegment(sketch, "E343.MirrorCS", {"start": v(-6.7, -42.7) * mm, "end": v(-7.46, -43.46) * mm});
            skLineSegment(sketch, "E344.MirrorCS", {"start": v(-22.14, -45) * mm, "end": v(-23.55, -45) * mm});
            skArc(sketch, "E345.MirrorCS", {"start": v(-41.98, 5) * mm, "mid": v(-41.05, 4.38) * mm, "end": v(-41.27, 3.3) * mm});
            skLineSegment(sketch, "E346.MirrorCS", {"start": v(-43.4, 5) * mm, "end": v(-41.98, 5) * mm});
            skLineSegment(sketch, "E347.MirrorCS", {"start": v(-39.1, -45) * mm, "end": v(-40.5, -45) * mm});
            skLineSegment(sketch, "E348.MirrorCS", {"start": v(-51.87, 5) * mm, "end": v(-50.46, 5) * mm});
            skArc(sketch, "E349.MirrorCS", {"start": v(-6.7, -0.3) * mm, "mid": v(-5.62, -0.1) * mm, "end": v(-5, -1.01) * mm});
            skArc(sketch, "E350.MirrorCS", {"start": v(-6.7, -25.75) * mm, "mid": v(-5.62, -25.53) * mm, "end": v(-5, -26.45) * mm});
            skLineSegment(sketch, "E351.MirrorCS", {"start": v(-5, -9.5) * mm, "end": v(-5, -10.9) * mm});
            skArc(sketch, "E352.MirrorCS", {"start": v(-6.7, -42.7) * mm, "mid": v(-5.62, -42.5) * mm, "end": v(-5, -43.41) * mm});
            skArc(sketch, "E353.MirrorCS", {"start": v(-65.95, -45) * mm, "mid": v(-66.87, -44.38) * mm, "end": v(-66.65, -43.3) * mm});
            skArc(sketch, "E354.MirrorCS", {"start": v(-25.02, 5) * mm, "mid": v(-24.1, 4.38) * mm, "end": v(-24.3, 3.3) * mm});
            skArc(sketch, "E355.MirrorCS", {"start": v(-40.5, -45) * mm, "mid": v(-41.43, -44.38) * mm, "end": v(-41.21, -43.3) * mm});
            skLineSegment(sketch, "E356.MirrorCS", {"start": v(-68.83, 5) * mm, "end": v(-67.42, 5) * mm});
            skLineSegment(sketch, "E357.MirrorCS", {"start": v(-60.77, 5) * mm, "end": v(-72.6, -6.84) * mm});
            skPoint(sketch, "E358.MirrorP", {"position": v(-72.6, -11.08) * mm});
            skArc(sketch, "E359.MirrorCS", {"start": v(-71.28, -18.24) * mm, "mid": v(-72.7, -18.52) * mm, "end": v(-73.5, -17.32) * mm});
            skPoint(sketch, "E360.MirrorP", {"position": v(-73.5, -45) * mm});
            skPoint(sketch, "E361.MirrorP", {"position": v(-26.85, 5) * mm});
            skPoint(sketch, "E362.MirrorP", {"position": v(-60.77, 5) * mm});
            skPoint(sketch, "E363.MirrorP", {"position": v(-72.6, -36.52) * mm});
            skPoint(sketch, "E364.MirrorP", {"position": v(-73.5, -16.21) * mm});
            skPoint(sketch, "E365.MirrorP", {"position": v(-72.6, -32.28) * mm});
            skPoint(sketch, "E366.MirrorP", {"position": v(-5, -7.08) * mm});
            skPoint(sketch, "E367.MirrorP", {"position": v(-5, -41) * mm});
            skPoint(sketch, "E368.MirrorP", {"position": v(-42.92, -45) * mm});
            skPoint(sketch, "E369.MirrorP", {"position": v(-64.12, -45) * mm});
            skPoint(sketch, "E370.MirrorP", {"position": v(-72.6, -28.04) * mm});
            skPoint(sketch, "E371.MirrorP", {"position": v(-22.6, 5) * mm});
            skPoint(sketch, "E372.MirrorP", {"position": v(-56.52, 5) * mm});
            skLineSegment(sketch, "E373.MirrorCS", {"start": v(-49.75, 3.3) * mm, "end": v(-71.28, -18.24) * mm});
            skLineSegment(sketch, "E374.MirrorCS", {"start": v(-69.54, 4.7) * mm, "end": v(-73.2, 1.04) * mm});
            skLineSegment(sketch, "E375.MirrorCS", {"start": v(-6.7, -8.79) * mm, "end": v(-41.21, -43.3) * mm});
            skLineSegment(sketch, "E376.MirrorCS", {"start": v(-5.3, -37.05) * mm, "end": v(-12.95, -44.7) * mm});
            skPoint(sketch, "E377.MirrorP", {"position": v(-5, -32.52) * mm});
            skPoint(sketch, "E378.MirrorP", {"position": v(-39.56, 5) * mm});
            skPoint(sketch, "E379.MirrorP", {"position": v(-69.25, 5) * mm});
            skPoint(sketch, "E380.MirrorP", {"position": v(-73.5, -7.73) * mm});
            skPoint(sketch, "E381.MirrorP", {"position": v(-73.5, -28.94) * mm});
            skPoint(sketch, "E382.MirrorP", {"position": v(-13.24, -45) * mm});
            skLineSegment(sketch, "E383.MirrorCS", {"start": v(-61.06, 4.7) * mm, "end": v(-73.2, -7.44) * mm});
            skLineSegment(sketch, "E384.MirrorCS", {"start": v(-10.17, 4.7) * mm, "end": v(-58.17, -43.3) * mm});
            skPoint(sketch, "E385.MirrorP", {"position": v(-5.64, 5) * mm});
            skPoint(sketch, "E386.MirrorP", {"position": v(-5, -15.56) * mm});
            skPoint(sketch, "E387.MirrorP", {"position": v(-47.16, -45) * mm});
            skPoint(sketch, "E388.MirrorP", {"position": v(-72.6, -45) * mm});
            skLineSegment(sketch, "E389.MirrorCS", {"start": v(-15.83, 3.3) * mm, "end": v(-63.83, -44.7) * mm});
            skPoint(sketch, "E390.MirrorP", {"position": v(-14.12, 5) * mm});
            skLineSegment(sketch, "E391.MirrorCS", {"start": v(-52.58, 4.7) * mm, "end": v(-73.2, -15.92) * mm});
            skPoint(sketch, "E392.MirrorP", {"position": v(-48.04, 5) * mm});
            skLineSegment(sketch, "E393.MirrorCS", {"start": v(-6.7, -0.3) * mm, "end": v(-49.7, -43.3) * mm});
            skPoint(sketch, "E394.MirrorP", {"position": v(-35.33, 5) * mm});
            skPoint(sketch, "E395.MirrorP", {"position": v(-43.8, 5) * mm});
            skPoint(sketch, "E396.MirrorP", {"position": v(-5, -2.84) * mm});
            skLineSegment(sketch, "E397.MirrorCS", {"start": v(-6.7, -17.27) * mm, "end": v(-32.73, -43.3) * mm});
            skLineSegment(sketch, "E398.MirrorCS", {"start": v(-32.79, 3.3) * mm, "end": v(-71.8, -35.71) * mm});
            skLineSegment(sketch, "E399.MirrorCS", {"start": v(-7.35, 3.3) * mm, "end": v(-55.35, -44.7) * mm});
            skPoint(sketch, "E400.MirrorP", {"position": v(-17.48, -45) * mm});
            skPoint(sketch, "E401.MirrorP", {"position": v(-73.5, 0.75) * mm});
            skPoint(sketch, "E402.MirrorP", {"position": v(-52.29, 5) * mm});
            skPoint(sketch, "E403.MirrorP", {"position": v(-72.6, -23.8) * mm});
            skPoint(sketch, "E404.MirrorP", {"position": v(-18.36, 5) * mm});
            skPoint(sketch, "E405.MirrorP", {"position": v(-5, -11.32) * mm});
            skPoint(sketch, "E406.MirrorP", {"position": v(-72.6, -19.56) * mm});
            skLineSegment(sketch, "E407.MirrorCS", {"start": v(-5.3, -3.13) * mm, "end": v(-46.87, -44.7) * mm});
            skPoint(sketch, "E408.MirrorP", {"position": v(-9.88, 5) * mm});
            skPoint(sketch, "E409.MirrorP", {"position": v(-31.08, 5) * mm});
            skPoint(sketch, "E410.MirrorP", {"position": v(-9, -45) * mm});
            skPoint(sketch, "E411.MirrorP", {"position": v(-5, -28.28) * mm});
            skLineSegment(sketch, "E412.MirrorCS", {"start": v(-27.14, 4.7) * mm, "end": v(-73.2, -41.36) * mm});
            skPoint(sketch, "E413.MirrorP", {"position": v(-73.5, -24.7) * mm});
            skPoint(sketch, "E414.MirrorP", {"position": v(-21.72, -45) * mm});
            skLineSegment(sketch, "E415.MirrorCS", {"start": v(-35.62, 4.7) * mm, "end": v(-73.2, -32.88) * mm});
            skPoint(sketch, "E416.MirrorP", {"position": v(-5, -36.76) * mm});
            skLineSegment(sketch, "E417.MirrorCS", {"start": v(-5, -19.8) * mm, "end": v(-29.9, -44.7) * mm});
            skLineSegment(sketch, "E418.MirrorCS", {"start": v(-5.3, -11.61) * mm, "end": v(-38.39, -44.7) * mm});
            skPoint(sketch, "E419.MirrorP", {"position": v(-30.2, -45) * mm});
            skPoint(sketch, "E420.MirrorP", {"position": v(-73.5, -3.5) * mm});
            skPoint(sketch, "E421.MirrorP", {"position": v(-73.5, -33.17) * mm});
            skPoint(sketch, "E422.MirrorP", {"position": v(-55.64, -45) * mm});
            skPoint(sketch, "E423.MirrorP", {"position": v(-5, 1.4) * mm});
            skLineSegment(sketch, "E424.MirrorCS", {"start": v(-5.3, -28.57) * mm, "end": v(-21.43, -44.7) * mm});
            skPoint(sketch, "E425.MirrorP", {"position": v(-25.96, -45) * mm});
            skLineSegment(sketch, "E426.MirrorCS", {"start": v(-66.7, 3.3) * mm, "end": v(-71.8, -1.8) * mm});
            skLineSegment(sketch, "E427.MirrorCS", {"start": v(-18.65, 4.7) * mm, "end": v(-66.65, -43.3) * mm});
            skPoint(sketch, "E428.MirrorP", {"position": v(-65, 5) * mm});
            skPoint(sketch, "E429.MirrorP", {"position": v(-73.5, -11.98) * mm});
            skPoint(sketch, "E430.MirrorP", {"position": v(-72.6, -40.76) * mm});
            skPoint(sketch, "E431.MirrorP", {"position": v(-72.6, -6.84) * mm});
            skLineSegment(sketch, "E432.MirrorCS", {"start": v(-6.7, -34.23) * mm, "end": v(-15.77, -43.3) * mm});
            skPoint(sketch, "E433.MirrorP", {"position": v(-51.4, -45) * mm});
            skPoint(sketch, "E434.MirrorP", {"position": v(-73.5, -41.65) * mm});
            skPoint(sketch, "E435.MirrorP", {"position": v(-73.5, -37.42) * mm});
            skPoint(sketch, "E436.MirrorP", {"position": v(-73.5, -20.46) * mm});
            skLineSegment(sketch, "E437.MirrorCS", {"start": v(-44.1, 4.7) * mm, "end": v(-73.2, -24.4) * mm});
            skLineSegment(sketch, "E438.MirrorCS", {"start": v(-24.3, 3.3) * mm, "end": v(-72.3, -44.7) * mm});
            skPoint(sketch, "E439.MirrorP", {"position": v(-68.36, -45) * mm});
            skPoint(sketch, "E440.MirrorP", {"position": v(-72.6, 1.64) * mm});
            skPoint(sketch, "E441.MirrorP", {"position": v(-5, -45) * mm});
            skPoint(sketch, "E442.MirrorP", {"position": v(-34.44, -45) * mm});
            skPoint(sketch, "E443.MirrorP", {"position": v(-59.88, -45) * mm});
            skPoint(sketch, "E444.MirrorP", {"position": v(-5, -24.04) * mm});
            skLineSegment(sketch, "E445.MirrorCS", {"start": v(-58.23, 3.3) * mm, "end": v(-71.62, -10.1) * mm});
            skLineSegment(sketch, "E446.MirrorCS", {"start": v(-41.27, 3.3) * mm, "end": v(-71.8, -27.23) * mm});
            skPoint(sketch, "E447.MirrorP", {"position": v(-72.6, -15.32) * mm});
            skLineSegment(sketch, "E448.MirrorCS", {"start": v(-6.7, -25.75) * mm, "end": v(-24.25, -43.3) * mm});
            skPoint(sketch, "E449.MirrorP", {"position": v(-38.68, -45) * mm});
            skPoint(sketch, "E450.MirrorP", {"position": v(-72.6, -2.6) * mm});
            skSolve(sketch);
        }
        {
            var Q0;
            Q0=makeQuery(id+"F10.imprint","IMPRINT",FACE,{"disambiguationData":[TD([[makeQuery(id+"F10.imprint","IMPRINT",EDGE,{"derivedFrom":sQuery(id+"F10.wireOp",EDGE,"E159.0")}),1.0]])]});
            var Q1;
            Q1=makeQuery(id+"F10.imprint","IMPRINT",FACE,{"disambiguationData":[TD([[makeQuery(id+"F10.imprint","IMPRINT",EDGE,{"derivedFrom":sQuery(id+"F10.wireOp",EDGE,"E165.0")}),1.0]])]});
            var Q2;
            Q2=makeQuery(id+"F10.imprint","IMPRINT",FACE,{"disambiguationData":[TD([[makeQuery(id+"F10.imprint","IMPRINT",EDGE,{"derivedFrom":sQuery(id+"F10.wireOp",EDGE,"E166.1.0.1")}),1.0]])]});
            var Q3;
            Q3=makeQuery(id+"F10.imprint","IMPRINT",FACE,{"disambiguationData":[TD([[makeQuery(id+"F10.imprint","IMPRINT",EDGE,{"derivedFrom":sQuery(id+"F10.wireOp",EDGE,"E166.2.0.1")}),1.0]])]});
            var Q4;
            Q4=makeQuery(id+"F10.imprint","IMPRINT",FACE,{"disambiguationData":[TD([[makeQuery(id+"F10.imprint","IMPRINT",EDGE,{"derivedFrom":sQuery(id+"F10.wireOp",EDGE,"E166.3.0.1")}),1.0]])]});
            var Q5;
            Q5=makeQuery(id+"F10.imprint","IMPRINT",FACE,{"disambiguationData":[TD([[makeQuery(id+"F10.imprint","IMPRINT",EDGE,{"derivedFrom":sQuery(id+"F10.wireOp",EDGE,"E161.0")}),1.0]])]});
            var Q6;
            Q6=makeQuery(id+"F10.imprint","IMPRINT",FACE,{"disambiguationData":[TD([[makeQuery(id+"F10.imprint","IMPRINT",EDGE,{"derivedFrom":sQuery(id+"F10.wireOp",EDGE,"E166.5.0.1")}),1.0]])]});
            var Q7;
            Q7=makeQuery(id+"F10.imprint","IMPRINT",FACE,{"disambiguationData":[TD([[makeQuery(id+"F10.imprint","IMPRINT",EDGE,{"derivedFrom":sQuery(id+"F10.wireOp",EDGE,"E166.6.0.1")}),1.0]])]});
            var Q8;
            {var subQ5=sQuery(id+"F10.wireOp",EDGE,"E166.7.0.1");Q8=makeQuery(id+"F10.imprint","IMPRINT",FACE,{"disambiguationData":[TD([[makeQuery(id+"F10.imprint","IMPRINT",EDGE,{"derivedFrom":subQ5}),1.0]])]});}
            var Q9;
            Q9=makeQuery(id+"F10.imprint","IMPRINT",FACE,{"disambiguationData":[TD([[makeQuery(id+"F10.imprint","IMPRINT",EDGE,{"derivedFrom":sQuery(id+"F10.wireOp",EDGE,"E170.MirrorCS")}),1.0]])]});
            var Q10;
            Q10=makeQuery(id+"F10.imprint","IMPRINT",FACE,{"disambiguationData":[TD([[makeQuery(id+"F10.imprint","IMPRINT",EDGE,{"derivedFrom":sQuery(id+"F10.wireOp",EDGE,"E172.MirrorCS")}),1.0]])]});
            var Q11;
            Q11=makeQuery(id+"F10.imprint","IMPRINT",FACE,{"disambiguationData":[TD([[makeQuery(id+"F10.imprint","IMPRINT",EDGE,{"derivedFrom":sQuery(id+"F10.wireOp",EDGE,"E174.MirrorCS")}),1.0]])]});
            var Q12;
            Q12=makeQuery(id+"F10.imprint","IMPRINT",FACE,{"disambiguationData":[TD([[makeQuery(id+"F10.imprint","IMPRINT",EDGE,{"derivedFrom":sQuery(id+"F10.wireOp",EDGE,"E177.MirrorCS")}),1.0]])]});
            var Q13;
            Q13=makeQuery(id+"F10.imprint","IMPRINT",FACE,{"disambiguationData":[TD([[makeQuery(id+"F10.imprint","IMPRINT",EDGE,{"derivedFrom":sQuery(id+"F10.wireOp",EDGE,"E162.trimOffspring")}),1.0]])]});
            extrude(context, id + "F11", {"entities" : qUnion([Q0, Q1, Q2, Q3, Q4, Q5, Q6, Q7, Q8, Q9, Q10, Q11, Q12, Q13]), "operationType" : NewBodyOperationType.REMOVE, "oppositeDirection" : true, "depth" : 25 * mm, "offsetDistance" : 25 * mm});
        }
        {
            var Q0;
            Q0=makeQuery(id+"F10.imprint","IMPRINT",FACE,{"disambiguationData":[TD([[makeQuery(id+"F10.imprint","IMPRINT",EDGE,{"derivedFrom":sQuery(id+"F10.wireOp",EDGE,"E277.MirrorCS")}),-1.0]])]});
            var Q1;
            {var subQ1=sQuery(id+"F10.wireOp",EDGE,"E275.MirrorCS");Q1=makeQuery(id+"F10.imprint","IMPRINT",FACE,{"disambiguationData":[TD([[makeQuery(id+"F10.imprint","IMPRINT",EDGE,{"derivedFrom":subQ1}),-1.0]])]});}
            var Q2;
            Q2=makeQuery(id+"F10.imprint","IMPRINT",FACE,{"disambiguationData":[TD([[makeQuery(id+"F10.imprint","IMPRINT",EDGE,{"derivedFrom":sQuery(id+"F10.wireOp",EDGE,"E278.MirrorCS")}),-1.0]])]});
            var Q3;
            Q3=makeQuery(id+"F10.imprint","IMPRINT",FACE,{"disambiguationData":[TD([[makeQuery(id+"F10.imprint","IMPRINT",EDGE,{"derivedFrom":sQuery(id+"F10.wireOp",EDGE,"E282.MirrorCS")}),-1.0]])]});
            var Q4;
            Q4=makeQuery(id+"F10.imprint","IMPRINT",FACE,{"disambiguationData":[TD([[makeQuery(id+"F10.imprint","IMPRINT",EDGE,{"derivedFrom":sQuery(id+"F10.wireOp",EDGE,"E283.MirrorCS")}),1.0]])]});
            var Q5;
            Q5=makeQuery(id+"F10.imprint","IMPRINT",FACE,{"disambiguationData":[TD([[makeQuery(id+"F10.imprint","IMPRINT",EDGE,{"derivedFrom":sQuery(id+"F10.wireOp",EDGE,"E276.MirrorCS")}),-1.0]])]});
            var Q6;
            Q6=makeQuery(id+"F10.imprint","IMPRINT",FACE,{"disambiguationData":[TD([[makeQuery(id+"F10.imprint","IMPRINT",EDGE,{"derivedFrom":sQuery(id+"F10.wireOp",EDGE,"E292.MirrorCS")}),-1.0]])]});
            var Q7;
            Q7=makeQuery(id+"F10.imprint","IMPRINT",FACE,{"disambiguationData":[TD([[makeQuery(id+"F10.imprint","IMPRINT",EDGE,{"derivedFrom":sQuery(id+"F10.wireOp",EDGE,"E301.MirrorCS")}),-1.0]])]});
            var Q8;
            Q8=makeQuery(id+"F10.imprint","IMPRINT",FACE,{"disambiguationData":[TD([[makeQuery(id+"F10.imprint","IMPRINT",EDGE,{"derivedFrom":sQuery(id+"F10.wireOp",EDGE,"E289.MirrorCS")}),-1.0]])]});
            var Q9;
            Q9=makeQuery(id+"F10.imprint","IMPRINT",FACE,{"disambiguationData":[TD([[makeQuery(id+"F10.imprint","IMPRINT",EDGE,{"derivedFrom":sQuery(id+"F10.wireOp",EDGE,"E290.MirrorCS")}),-1.0]])]});
            var Q10;
            Q10=makeQuery(id+"F10.imprint","IMPRINT",FACE,{"disambiguationData":[TD([[makeQuery(id+"F10.imprint","IMPRINT",EDGE,{"derivedFrom":sQuery(id+"F10.wireOp",EDGE,"E281.MirrorCS")}),-1.0]])]});
            var Q11;
            Q11=makeQuery(id+"F10.imprint","IMPRINT",FACE,{"disambiguationData":[TD([[makeQuery(id+"F10.imprint","IMPRINT",EDGE,{"derivedFrom":sQuery(id+"F10.wireOp",EDGE,"E288.MirrorCS")}),-1.0]])]});
            var Q12;
            Q12=makeQuery(id+"F10.imprint","IMPRINT",FACE,{"disambiguationData":[TD([[makeQuery(id+"F10.imprint","IMPRINT",EDGE,{"derivedFrom":sQuery(id+"F10.wireOp",EDGE,"E299.MirrorCS")}),-1.0]])]});
            var Q13;
            Q13=makeQuery(id+"F10.imprint","IMPRINT",FACE,{"disambiguationData":[TD([[makeQuery(id+"F10.imprint","IMPRINT",EDGE,{"derivedFrom":sQuery(id+"F10.wireOp",EDGE,"E293.MirrorCS")}),-1.0]])]});
            extrude(context, id + "F12", {"entities" : qUnion([Q0, Q1, Q2, Q3, Q4, Q5, Q6, Q7, Q8, Q9, Q10, Q11, Q12, Q13]), "operationType" : NewBodyOperationType.REMOVE, "oppositeDirection" : true, "depth" : 25 * mm, "offsetDistance" : 25 * mm});
        }
    });
